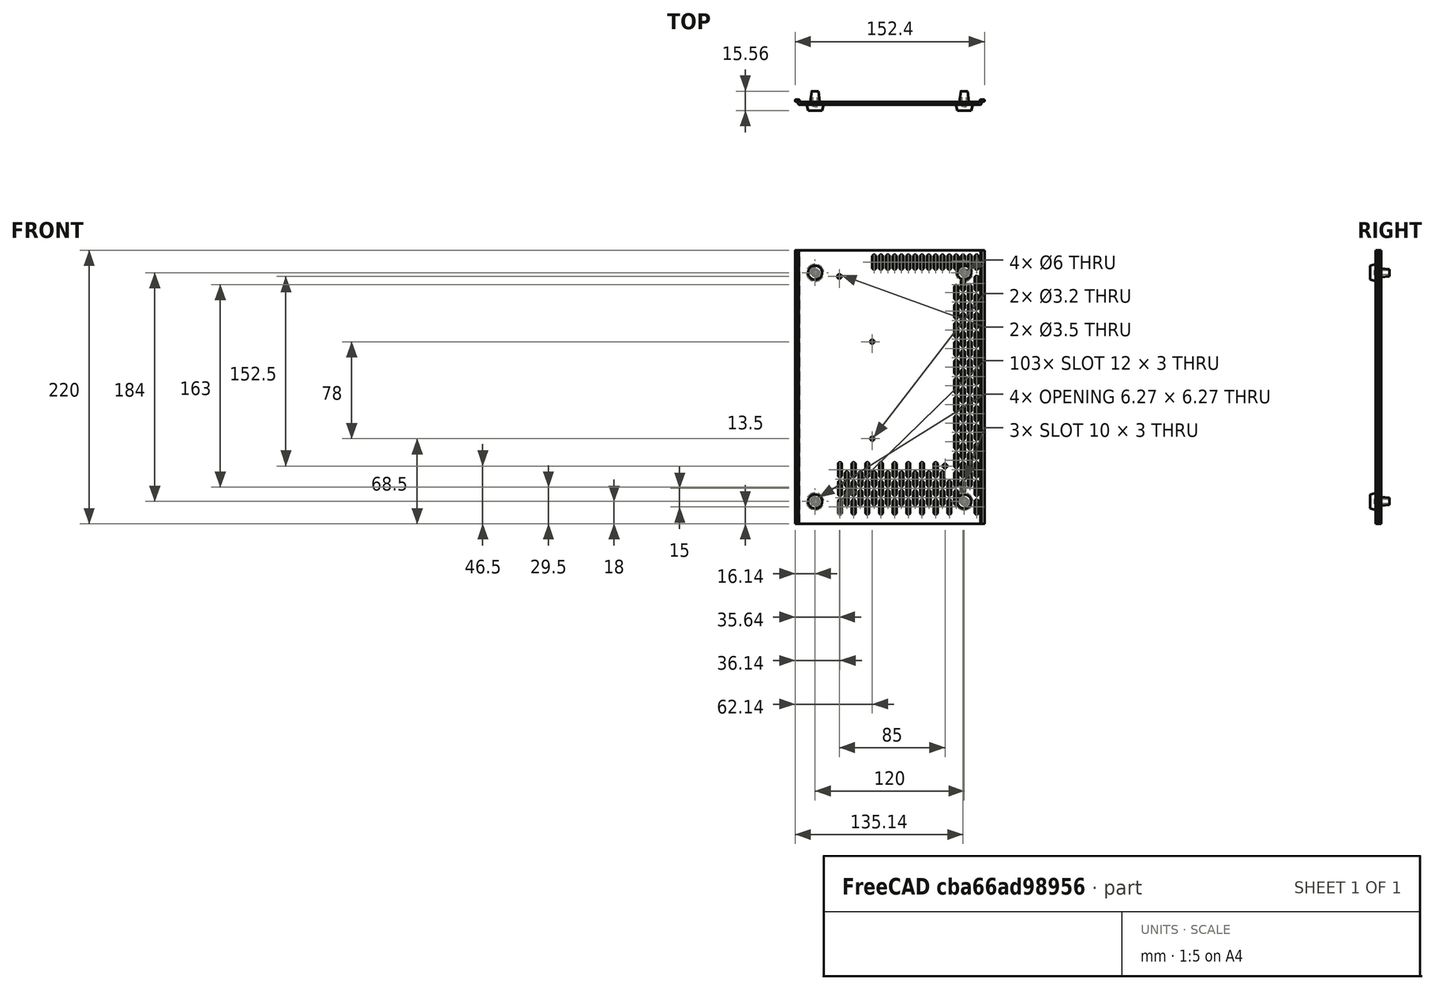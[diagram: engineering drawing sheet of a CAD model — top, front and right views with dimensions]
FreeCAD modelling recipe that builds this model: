
FCSTD DOCUMENT  (FreeCAD 0.19R)
Label: 3d_assm_bottomplate_w_feet
License: All rights reserved
LicenseURL: http://en.wikipedia.org/wiki/All_rights_reserved
objects: Sketcher::SketchObject×5, Part::Feature×5, App::DocumentObjectGroup×1
note: 10 computed .brp shape members not serialized (recipe doc carries the construction recipe); baked Part::Feature solids carry a one-line shape summary decoded from their .brp

FEATURE [Sketcher::SketchObject] Sketch008  label="Sketch008-Front_vent_slots"
  FullyConstrained = true
  MapMode = 5
  Placement = pos=(-1.0955e-12,2.25,0) rot=(0,0.707107,0.707107;3.14159rad)
  sketch-geometry (112):
    g0: LineSegment StartX=26 StartY=105 StartZ=0 EndX=-70 EndY=105 EndZ=0
    g1: LineSegment StartX=-70 StartY=96 StartZ=0 EndX=26 EndY=96 EndZ=0
    g2: LineSegment StartX=-70 StartY=105 StartZ=0 EndX=-70 EndY=96 EndZ=0
    g3: LineSegment StartX=-64.5 StartY=105 StartZ=0 EndX=-64.5 EndY=96 EndZ=0
    g4: LineSegment StartX=-70 StartY=105 StartZ=0 EndX=-64.5 EndY=105 EndZ=0
    g5: LineSegment StartX=-59 StartY=105 StartZ=0 EndX=-59 EndY=96 EndZ=0
    g6: LineSegment StartX=-64.5 StartY=105 StartZ=0 EndX=-59 EndY=105 EndZ=0
    g7: LineSegment StartX=-53.5 StartY=105 StartZ=0 EndX=-53.5 EndY=96 EndZ=0
    g8: LineSegment StartX=-59 StartY=105 StartZ=0 EndX=-53.5 EndY=105 EndZ=0
    g9: LineSegment StartX=-48 StartY=105 StartZ=0 EndX=-48 EndY=96 EndZ=0
    g10: LineSegment StartX=-53.5 StartY=105 StartZ=0 EndX=-48 EndY=105 EndZ=0
    g11: LineSegment StartX=-42.5 StartY=105 StartZ=0 EndX=-42.5 EndY=96 EndZ=0
    g12: LineSegment StartX=-48 StartY=105 StartZ=0 EndX=-42.5 EndY=105 EndZ=0
    g13: LineSegment StartX=-37 StartY=105 StartZ=0 EndX=-37 EndY=96 EndZ=0
    g14: LineSegment StartX=-42.5 StartY=105 StartZ=0 EndX=-37 EndY=105 EndZ=0
    g15: LineSegment StartX=-31.5 StartY=105 StartZ=0 EndX=-31.5 EndY=96 EndZ=0
    g16: LineSegment StartX=-37 StartY=105 StartZ=0 EndX=-31.5 EndY=105 EndZ=0
    g17: LineSegment StartX=-26 StartY=105 StartZ=0 EndX=-26 EndY=96 EndZ=0
    g18: LineSegment StartX=-31.5 StartY=105 StartZ=0 EndX=-26 EndY=105 EndZ=0
    g19: LineSegment StartX=-20.5 StartY=105 StartZ=0 EndX=-20.5 EndY=96 EndZ=0
    g20: LineSegment StartX=-26 StartY=105 StartZ=0 EndX=-20.5 EndY=105 EndZ=0
    g21: LineSegment StartX=-15 StartY=105 StartZ=0 EndX=-15 EndY=96 EndZ=0
    g22: LineSegment StartX=-20.5 StartY=105 StartZ=0 EndX=-15 EndY=105 EndZ=0
    g23: LineSegment StartX=-9.5 StartY=105 StartZ=0 EndX=-9.5 EndY=96 EndZ=0
    g24: LineSegment StartX=-15 StartY=105 StartZ=0 EndX=-9.5 EndY=105 EndZ=0
    g25: LineSegment StartX=-4 StartY=105 StartZ=0 EndX=-4 EndY=96 EndZ=0
    g26: LineSegment StartX=-9.5 StartY=105 StartZ=0 EndX=-4 EndY=105 EndZ=0
    g27: LineSegment StartX=1.5 StartY=105 StartZ=0 EndX=1.5 EndY=96 EndZ=0
    g28: LineSegment StartX=-4 StartY=105 StartZ=0 EndX=1.5 EndY=105 EndZ=0
    g29: LineSegment StartX=7 StartY=105 StartZ=0 EndX=7 EndY=96 EndZ=0
    g30: LineSegment StartX=1.5 StartY=105 StartZ=0 EndX=7 EndY=105 EndZ=0
    g31: LineSegment StartX=12.5 StartY=105 StartZ=0 EndX=12.5 EndY=96 EndZ=0
    g32: LineSegment StartX=7 StartY=105 StartZ=0 EndX=12.5 EndY=105 EndZ=0
    g33: ArcOfCircle CenterX=-70 CenterY=105 CenterZ=0 NormalX=0 NormalY=0 NormalZ=1 AngleXU=0 Radius=1.5 StartAngle=-3.6e-15 EndAngle=3.14159
    g34: ArcOfCircle CenterX=-70 CenterY=96 CenterZ=0 NormalX=0 NormalY=0 NormalZ=1 AngleXU=0 Radius=1.5 StartAngle=3.14159 EndAngle=6.28319
    g35: LineSegment StartX=-71.5 StartY=105 StartZ=0 EndX=-71.5 EndY=96 EndZ=0
    g36: LineSegment StartX=-68.5 StartY=105 StartZ=0 EndX=-68.5 EndY=96 EndZ=0
    g37: ArcOfCircle CenterX=-64.5 CenterY=105 CenterZ=0 NormalX=0 NormalY=0 NormalZ=1 AngleXU=0 Radius=1.5 StartAngle=4.5e-15 EndAngle=3.14159
    g38: ArcOfCircle CenterX=-64.5 CenterY=96 CenterZ=0 NormalX=0 NormalY=0 NormalZ=1 AngleXU=0 Radius=1.5 StartAngle=3.14159 EndAngle=6.28319
    g39: LineSegment StartX=-66 StartY=105 StartZ=0 EndX=-66 EndY=96 EndZ=0
    g40: LineSegment StartX=-63 StartY=105 StartZ=0 EndX=-63 EndY=96 EndZ=0
    g41: LineSegment StartX=-68.5 StartY=105 StartZ=0 EndX=-63 EndY=105 EndZ=0
    g42: ArcOfCircle CenterX=-59 CenterY=105 CenterZ=0 NormalX=0 NormalY=0 NormalZ=1 AngleXU=0 Radius=1.5 StartAngle=3.9e-15 EndAngle=3.14159
    g43: ArcOfCircle CenterX=-59 CenterY=98 CenterZ=0 NormalX=0 NormalY=0 NormalZ=1 AngleXU=0 Radius=1.5 StartAngle=3.14159 EndAngle=6.28319
    g44: LineSegment StartX=-60.5 StartY=105 StartZ=0 EndX=-60.5 EndY=98 EndZ=0
    g45: LineSegment StartX=-57.5 StartY=105 StartZ=0 EndX=-57.5 EndY=98 EndZ=0
    g46: LineSegment StartX=-63 StartY=105 StartZ=0 EndX=-57.5 EndY=105 EndZ=0
    g47: ArcOfCircle CenterX=-53.5 CenterY=105 CenterZ=0 NormalX=0 NormalY=0 NormalZ=1 AngleXU=0 Radius=1.5 StartAngle=3e-16 EndAngle=3.14159
    g48: ArcOfCircle CenterX=-53.5 CenterY=96 CenterZ=0 NormalX=0 NormalY=0 NormalZ=1 AngleXU=0 Radius=1.5 StartAngle=3.14159 EndAngle=6.28319
    g49: LineSegment StartX=-55 StartY=105 StartZ=0 EndX=-55 EndY=96 EndZ=0
    g50: LineSegment StartX=-52 StartY=105 StartZ=0 EndX=-52 EndY=96 EndZ=0
    g51: LineSegment StartX=-57.5 StartY=105 StartZ=0 EndX=-52 EndY=105 EndZ=0
    g52: ArcOfCircle CenterX=-48 CenterY=105 CenterZ=0 NormalX=0 NormalY=0 NormalZ=1 AngleXU=0 Radius=1.5 StartAngle=-2.7e-15 EndAngle=3.14159
    g53: ArcOfCircle CenterX=-48 CenterY=96 CenterZ=0 NormalX=0 NormalY=0 NormalZ=1 AngleXU=0 Radius=1.5 StartAngle=3.14159 EndAngle=6.28319
    g54: LineSegment StartX=-49.5 StartY=105 StartZ=0 EndX=-49.5 EndY=96 EndZ=0
    g55: LineSegment StartX=-46.5 StartY=105 StartZ=0 EndX=-46.5 EndY=96 EndZ=0
    g56: LineSegment StartX=-52 StartY=105 StartZ=0 EndX=-46.5 EndY=105 EndZ=0
    g57: ArcOfCircle CenterX=-42.5 CenterY=105 CenterZ=0 NormalX=0 NormalY=0 NormalZ=1 AngleXU=0 Radius=1.5 StartAngle=1.8e-15 EndAngle=3.14159
    g58: ArcOfCircle CenterX=-42.5 CenterY=96 CenterZ=0 NormalX=0 NormalY=0 NormalZ=1 AngleXU=0 Radius=1.5 StartAngle=3.14159 EndAngle=6.28319
    g59: LineSegment StartX=-44 StartY=105 StartZ=0 EndX=-44 EndY=96 EndZ=0
    g60: LineSegment StartX=-41 StartY=105 StartZ=0 EndX=-41 EndY=96 EndZ=0
    g61: LineSegment StartX=-46.5 StartY=105 StartZ=0 EndX=-41 EndY=105 EndZ=0
    g62: ArcOfCircle CenterX=-37 CenterY=105 CenterZ=0 NormalX=0 NormalY=0 NormalZ=1 AngleXU=0 Radius=1.5 StartAngle=-9e-16 EndAngle=3.14159
    g63: ArcOfCircle CenterX=-37 CenterY=96 CenterZ=0 NormalX=0 NormalY=0 NormalZ=1 AngleXU=0 Radius=1.5 StartAngle=3.14159 EndAngle=6.28319
    g64: LineSegment StartX=-38.5 StartY=105 StartZ=0 EndX=-38.5 EndY=96 EndZ=0
    g65: LineSegment StartX=-35.5 StartY=105 StartZ=0 EndX=-35.5 EndY=96 EndZ=0
    g66: LineSegment StartX=-41 StartY=105 StartZ=0 EndX=-35.5 EndY=105 EndZ=0
    g67: ArcOfCircle CenterX=-31.5 CenterY=105 CenterZ=0 NormalX=0 NormalY=0 NormalZ=1 AngleXU=0 Radius=1.5 StartAngle=-2.7e-15 EndAngle=3.14159
    g68: ArcOfCircle CenterX=-31.5 CenterY=96 CenterZ=0 NormalX=0 NormalY=0 NormalZ=1 AngleXU=0 Radius=1.5 StartAngle=3.14159 EndAngle=6.28319
    g69: LineSegment StartX=-33 StartY=105 StartZ=0 EndX=-33 EndY=96 EndZ=0
    g70: LineSegment StartX=-30 StartY=105 StartZ=0 EndX=-30 EndY=96 EndZ=0
    g71: LineSegment StartX=-35.5 StartY=105 StartZ=0 EndX=-30 EndY=105 EndZ=0
    g72: ArcOfCircle CenterX=-26 CenterY=105 CenterZ=0 NormalX=0 NormalY=0 NormalZ=1 AngleXU=0 Radius=1.5 StartAngle=-2.7e-15 EndAngle=3.14159
    g73: ArcOfCircle CenterX=-26 CenterY=96 CenterZ=0 NormalX=0 NormalY=0 NormalZ=1 AngleXU=0 Radius=1.5 StartAngle=3.14159 EndAngle=6.28319
    g74: LineSegment StartX=-27.5 StartY=105 StartZ=0 EndX=-27.5 EndY=96 EndZ=0
    g75: LineSegment StartX=-24.5 StartY=105 StartZ=0 EndX=-24.5 EndY=96 EndZ=0
    g76: LineSegment StartX=-30 StartY=105 StartZ=0 EndX=-24.5 EndY=105 EndZ=0
    g77: ArcOfCircle CenterX=-20.5 CenterY=105 CenterZ=0 NormalX=0 NormalY=0 NormalZ=1 AngleXU=0 Radius=1.5 StartAngle=-3.6e-15 EndAngle=3.14159
    g78: ArcOfCircle CenterX=-20.5 CenterY=96 CenterZ=0 NormalX=0 NormalY=0 NormalZ=1 AngleXU=0 Radius=1.5 StartAngle=3.14159 EndAngle=6.28319
    g79: LineSegment StartX=-22 StartY=105 StartZ=0 EndX=-22 EndY=96 EndZ=0
    g80: LineSegment StartX=-19 StartY=105 StartZ=0 EndX=-19 EndY=96 EndZ=0
    g81: LineSegment StartX=-24.5 StartY=105 StartZ=0 EndX=-19 EndY=105 EndZ=0
    g82: ArcOfCircle CenterX=-15 CenterY=105 CenterZ=0 NormalX=0 NormalY=0 NormalZ=1 AngleXU=0 Radius=1.5 StartAngle=2.4e-15 EndAngle=3.14159
    g83: ArcOfCircle CenterX=-15 CenterY=96 CenterZ=0 NormalX=0 NormalY=0 NormalZ=1 AngleXU=0 Radius=1.5 StartAngle=3.14159 EndAngle=6.28319
    g84: LineSegment StartX=-16.5 StartY=105 StartZ=0 EndX=-16.5 EndY=96 EndZ=0
    g85: LineSegment StartX=-13.5 StartY=105 StartZ=0 EndX=-13.5 EndY=96 EndZ=0
    g86: LineSegment StartX=-19 StartY=105 StartZ=0 EndX=-13.5 EndY=105 EndZ=0
    g87: ArcOfCircle CenterX=-9.5 CenterY=105 CenterZ=0 NormalX=0 NormalY=0 NormalZ=1 AngleXU=0 Radius=1.5 StartAngle=2.7e-15 EndAngle=3.14159
    g88: ArcOfCircle CenterX=-9.5 CenterY=96 CenterZ=0 NormalX=0 NormalY=0 NormalZ=1 AngleXU=0 Radius=1.5 StartAngle=3.14159 EndAngle=6.28319
    g89: LineSegment StartX=-11 StartY=105 StartZ=0 EndX=-11 EndY=96 EndZ=0
    g90: LineSegment StartX=-8 StartY=105 StartZ=0 EndX=-8 EndY=96 EndZ=0
    g91: LineSegment StartX=-13.5 StartY=105 StartZ=0 EndX=-8 EndY=105 EndZ=0
    g92: ArcOfCircle CenterX=-4 CenterY=105 CenterZ=0 NormalX=0 NormalY=0 NormalZ=1 AngleXU=0 Radius=1.5 StartAngle=3e-15 EndAngle=3.14159
    g93: ArcOfCircle CenterX=-4 CenterY=96 CenterZ=0 NormalX=0 NormalY=0 NormalZ=1 AngleXU=0 Radius=1.5 StartAngle=3.14159 EndAngle=6.28319
    g94: LineSegment StartX=-5.5 StartY=105 StartZ=0 EndX=-5.5 EndY=96 EndZ=0
    g95: LineSegment StartX=-2.5 StartY=105 StartZ=0 EndX=-2.5 EndY=96 EndZ=0
    g96: LineSegment StartX=-8 StartY=105 StartZ=0 EndX=-2.5 EndY=105 EndZ=0
    g97: ArcOfCircle CenterX=1.5 CenterY=105 CenterZ=0 NormalX=0 NormalY=0 NormalZ=1 AngleXU=0 Radius=1.5 StartAngle=1.8e-15 EndAngle=3.14159
    g98: ArcOfCircle CenterX=1.5 CenterY=96 CenterZ=0 NormalX=0 NormalY=0 NormalZ=1 AngleXU=0 Radius=1.5 StartAngle=3.14159 EndAngle=6.28319
    g99: LineSegment StartX=6e-15 StartY=105 StartZ=0 EndX=6e-15 EndY=96 EndZ=0
    g100: LineSegment StartX=3 StartY=105 StartZ=0 EndX=3 EndY=96 EndZ=0
    g101: LineSegment StartX=-2.5 StartY=105 StartZ=0 EndX=3 EndY=105 EndZ=0
    g102: ArcOfCircle CenterX=7 CenterY=105 CenterZ=0 NormalX=0 NormalY=0 NormalZ=1 AngleXU=0 Radius=1.5 StartAngle=-4.4e-15 EndAngle=3.14159
    g103: ArcOfCircle CenterX=7 CenterY=96 CenterZ=0 NormalX=0 NormalY=0 NormalZ=1 AngleXU=0 Radius=1.5 StartAngle=3.14159 EndAngle=6.28319
    g104: LineSegment StartX=5.5 StartY=105 StartZ=0 EndX=5.5 EndY=96 EndZ=0
    g105: LineSegment StartX=8.5 StartY=105 StartZ=0 EndX=8.5 EndY=96 EndZ=0
    g106: LineSegment StartX=3 StartY=105 StartZ=0 EndX=8.5 EndY=105 EndZ=0
    g107: ArcOfCircle CenterX=12.5 CenterY=105 CenterZ=0 NormalX=0 NormalY=0 NormalZ=1 AngleXU=0 Radius=1.5 StartAngle=2.7e-15 EndAngle=3.14159
    g108: ArcOfCircle CenterX=12.5 CenterY=96 CenterZ=0 NormalX=0 NormalY=0 NormalZ=1 AngleXU=0 Radius=1.5 StartAngle=3.14159 EndAngle=6.28319
    g109: LineSegment StartX=11 StartY=105 StartZ=0 EndX=11 EndY=96 EndZ=0
    g110: LineSegment StartX=14 StartY=105 StartZ=0 EndX=14 EndY=96 EndZ=0
    g111: LineSegment StartX=8.5 StartY=105 StartZ=0 EndX=14 EndY=105 EndZ=0
  constraints (289):
    c: Horizontal(g0)
    c: Horizontal(g1)
    c: DistanceX(g0,g0) = 96
    c: DistanceX(g0,g-1) = 70
    c: Equal(g0,g1)
    c: Vertical(g1,g0)
    c: DistanceY(g1,g0) = 9
    c: Coincident(g2,g0)
    c: Coincident(g2,g1)
    c: Vertical(g3)
    c: Coincident(g2,g4)
    c: Coincident(g3,g4)
    c: Distance(g4) = 5.5
    c: Vertical(g5)
    c: Coincident(g3,g6)
    c: Coincident(g5,g6)
    c: Equal(g4,g6)
    c: Parallel(g6,g4)
    c: Vertical(g7)
    c: Coincident(g5,g8)
    c: Coincident(g7,g8)
    c: Equal(g4,g8)
    c: Parallel(g8,g4)
    c: Vertical(g9)
    c: Coincident(g7,g10)
    c: Coincident(g9,g10)
    c: Equal(g4,g10)
    c: Parallel(g10,g4)
    c: Vertical(g11)
    c: Coincident(g9,g12)
    c: Coincident(g11,g12)
    c: Equal(g4,g12)
    c: Parallel(g12,g4)
    c: Vertical(g13)
    c: Coincident(g11,g14)
    c: Coincident(g13,g14)
    c: Equal(g4,g14)
    c: Parallel(g14,g4)
    c: Vertical(g15)
    c: Coincident(g13,g16)
    c: Coincident(g15,g16)
    c: Equal(g4,g16)
    c: Parallel(g16,g4)
    c: Vertical(g17)
    c: Coincident(g15,g18)
    c: Coincident(g17,g18)
    c: Equal(g4,g18)
    c: Parallel(g18,g4)
    c: Vertical(g19)
    c: Coincident(g17,g20)
    c: Coincident(g19,g20)
    c: Equal(g4,g20)
    c: Parallel(g20,g4)
    c: Vertical(g21)
    c: Coincident(g19,g22)
    c: Coincident(g21,g22)
    c: Equal(g4,g22)
    c: Parallel(g22,g4)
    c: Vertical(g23)
    c: Coincident(g21,g24)
    c: Coincident(g23,g24)
    c: Equal(g4,g24)
    c: Parallel(g24,g4)
    c: Vertical(g25)
    c: Coincident(g23,g26)
    c: Coincident(g25,g26)
    c: Equal(g4,g26)
    c: Parallel(g26,g4)
    c: Vertical(g27)
    c: Coincident(g25,g28)
    c: Coincident(g27,g28)
    c: Equal(g4,g28)
    c: Parallel(g28,g4)
    c: Vertical(g29)
    c: Coincident(g27,g30)
    c: Coincident(g29,g30)
    c: Equal(g4,g30)
    c: Parallel(g30,g4)
    c: Vertical(g31)
    c: Coincident(g29,g32)
    c: Coincident(g31,g32)
    c: Equal(g4,g32)
    c: Parallel(g32,g4)
    c: Horizontal(g1,g3)
    c: Horizontal(g3,g5)
    c: Horizontal(g5,g7)
    c: Horizontal(g7,g9)
    c: Horizontal(g9,g11)
    c: Horizontal(g11,g13)
    c: Horizontal(g13,g15)
    c: Horizontal(g15,g17)
    c: Horizontal(g17,g19)
    c: Horizontal(g19,g21)
    c: Horizontal(g21,g23)
    c: Horizontal(g23,g25)
    c: Horizontal(g25,g27)
    c: Horizontal(g27,g29)
    c: Horizontal(g29,g31)
    c: Angle(g26) = 0
    c: Tangent(g33,g36) = 1.5708
    c: Tangent(g33,g35) = -1.5708
    c: Tangent(g35,g34) = -1.5708
    c: Tangent(g36,g34) = 1.5708
    c: Vertical(g35)
    c: Equal(g33,g34)
    c: Coincident(g33,g0)
    c: DistanceX(g33,g33) = 3
    c: Tangent(g37,g40) = 1.5708
    c: Tangent(g37,g39) = -1.5708
    c: Tangent(g39,g38) = -1.5708
    c: Tangent(g40,g38) = 1.5708
    c: Vertical(g39)
    c: Equal(g37,g38)
    c: Equal(g33,g37) = 3
    c: Coincident(g33,g41)
    c: Coincident(g37,g41)
    c: Distance(g41) = 5.5
    c: Angle(g41) = 0
    c: Tangent(g42,g45) = 1.5708
    c: Tangent(g42,g44) = -1.5708
    c: Tangent(g44,g43) = -1.5708
    c: Tangent(g45,g43) = 1.5708
    c: Vertical(g44)
    c: Equal(g42,g43)
    c: Equal(g33,g42) = 3
    c: Coincident(g37,g46)
    c: Coincident(g42,g46)
    c: Equal(g41,g46)
    c: Parallel(g46,g41)
    c: Tangent(g47,g50) = 1.5708
    c: Tangent(g47,g49) = -1.5708
    c: Tangent(g49,g48) = -1.5708
    c: Tangent(g50,g48) = 1.5708
    c: Vertical(g49)
    c: Equal(g47,g48)
    c: Equal(g33,g47) = 3
    c: Coincident(g42,g51)
    c: Coincident(g47,g51)
    c: Equal(g41,g51)
    c: Parallel(g51,g41)
    c: Tangent(g52,g55) = 1.5708
    c: Tangent(g52,g54) = -1.5708
    c: Tangent(g54,g53) = -1.5708
    c: Tangent(g55,g53) = 1.5708
    c: Vertical(g54)
    c: Equal(g52,g53)
    c: Equal(g33,g52) = 3
    c: Coincident(g47,g56)
    c: Coincident(g52,g56)
    c: Equal(g41,g56)
    c: Parallel(g56,g41)
    c: Tangent(g57,g60) = 1.5708
    c: Tangent(g57,g59) = -1.5708
    c: Tangent(g59,g58) = -1.5708
    c: Tangent(g60,g58) = 1.5708
    c: Vertical(g59)
    c: Equal(g57,g58)
    c: Equal(g33,g57) = 3
    c: Coincident(g52,g61)
    c: Coincident(g57,g61)
    c: Equal(g41,g61)
    c: Parallel(g61,g41)
    c: Tangent(g62,g65) = 1.5708
    c: Tangent(g62,g64) = -1.5708
    c: Tangent(g64,g63) = -1.5708
    c: Tangent(g65,g63) = 1.5708
    c: Vertical(g64)
    c: Equal(g62,g63)
    c: Equal(g33,g62) = 3
    c: Coincident(g57,g66)
    c: Coincident(g62,g66)
    c: Equal(g41,g66)
    c: Parallel(g66,g41)
    c: Tangent(g67,g70) = 1.5708
    c: Tangent(g67,g69) = -1.5708
    c: Tangent(g69,g68) = -1.5708
    c: Tangent(g70,g68) = 1.5708
    c: Vertical(g69)
    c: Equal(g67,g68)
    c: Equal(g33,g67) = 3
    c: Coincident(g62,g71)
    c: Coincident(g67,g71)
    c: Equal(g41,g71)
    c: Parallel(g71,g41)
    c: Tangent(g72,g75) = 1.5708
    c: Tangent(g72,g74) = -1.5708
    c: Tangent(g74,g73) = -1.5708
    c: Tangent(g75,g73) = 1.5708
    c: Vertical(g74)
    c: Equal(g72,g73)
    c: Equal(g33,g72) = 3
    c: Coincident(g67,g76)
    c: Coincident(g72,g76)
    c: Equal(g41,g76)
    c: Parallel(g76,g41)
    c: Tangent(g77,g80) = 1.5708
    c: Tangent(g77,g79) = -1.5708
    c: Tangent(g79,g78) = -1.5708
    c: Tangent(g80,g78) = 1.5708
    c: Vertical(g79)
    c: Equal(g77,g78)
    c: Equal(g33,g77) = 3
    c: Coincident(g72,g81)
    c: Coincident(g77,g81)
    c: Equal(g41,g81)
    c: Parallel(g81,g41)
    c: Tangent(g82,g85) = 1.5708
    c: Tangent(g82,g84) = -1.5708
    c: Tangent(g84,g83) = -1.5708
    c: Tangent(g85,g83) = 1.5708
    c: Vertical(g84)
    c: Equal(g82,g83)
    c: Equal(g33,g82) = 3
    c: Coincident(g77,g86)
    c: Coincident(g82,g86)
    c: Equal(g41,g86)
    c: Parallel(g86,g41)
    c: Tangent(g87,g90) = 1.5708
    c: Tangent(g87,g89) = -1.5708
    c: Tangent(g89,g88) = -1.5708
    c: Tangent(g90,g88) = 1.5708
    c: Vertical(g89)
    c: Equal(g87,g88)
    c: Equal(g33,g87) = 3
    c: Coincident(g82,g91)
    c: Coincident(g87,g91)
    c: Equal(g41,g91)
    c: Parallel(g91,g41)
    c: Tangent(g92,g95) = 1.5708
    c: Tangent(g92,g94) = -1.5708
    c: Tangent(g94,g93) = -1.5708
    c: Tangent(g95,g93) = 1.5708
    c: Vertical(g94)
    c: Equal(g92,g93)
    c: Equal(g33,g92) = 3
    c: Coincident(g87,g96)
    c: Coincident(g92,g96)
    c: Equal(g41,g96)
    c: Parallel(g96,g41)
    c: Tangent(g97,g100) = 1.5708
    c: Tangent(g97,g99) = -1.5708
    c: Tangent(g99,g98) = -1.5708
    c: Tangent(g100,g98) = 1.5708
    c: Vertical(g99)
    c: Equal(g97,g98)
    c: Equal(g33,g97) = 3
    c: Coincident(g92,g101)
    c: Coincident(g97,g101)
    c: Equal(g41,g101)
    c: Parallel(g101,g41)
    c: Tangent(g102,g105) = 1.5708
    c: Tangent(g102,g104) = -1.5708
    c: Tangent(g104,g103) = -1.5708
    c: Tangent(g105,g103) = 1.5708
    c: Vertical(g104)
    c: Equal(g102,g103)
    c: Equal(g33,g102) = 3
    c: Coincident(g97,g106)
    c: Coincident(g102,g106)
    c: Equal(g41,g106)
    c: Parallel(g106,g41)
    c: Tangent(g107,g110) = 1.5708
    c: Tangent(g107,g109) = -1.5708
    c: Tangent(g109,g108) = -1.5708
    c: Tangent(g110,g108) = 1.5708
    c: Vertical(g109)
    c: Equal(g107,g108)
    c: Equal(g33,g107) = 3
    c: Coincident(g102,g111)
    c: Coincident(g107,g111)
    c: Equal(g41,g111)
    c: Parallel(g111,g41)
    c: Horizontal(g48,g53)
    c: Horizontal(g53,g58)
    c: Horizontal(g58,g63)
    c: Horizontal(g63,g68)
    c: Horizontal(g68,g73)
    c: Horizontal(g73,g78)
    c: Horizontal(g78,g83)
    c: Horizontal(g83,g88)
    c: Horizontal(g88,g93)
    c: Horizontal(g93,g98)
    c: Horizontal(g98,g103)
    c: Horizontal(g103,g108)
    c: DistanceY(g-1,g0) = 105
    c: Horizontal(g108,g1)
    c: DistanceY(g38,g37) = 9
    c: Horizontal(g34,g48)
    c: DistanceY(g43,g42) = 7
FEATURE [Sketcher::SketchObject] Sketch009
  FullyConstrained = false
  MapMode = 5
  Placement = pos=(-1.0955e-12,2.25,0) rot=(0,0.707107,0.707107;3.14159rad)
  sketch-geometry (289):
    g0: LineSegment StartX=-70 StartY=73 StartZ=0 EndX=-31.4704 EndY=73 EndZ=0
    g1: LineSegment StartX=-68.5 StartY=64 StartZ=0 EndX=-33.9766 EndY=64 EndZ=0
    g2: LineSegment StartX=-64.5 StartY=80.5 StartZ=0 EndX=-38.6885 EndY=80.5 EndZ=0
    g3: LineSegment StartX=-63 StartY=71.5 StartZ=0 EndX=-33.4278 EndY=71.5 EndZ=0
    g4: ArcOfCircle CenterX=-70 CenterY=73 CenterZ=0 NormalX=0 NormalY=0 NormalZ=1 AngleXU=0 Radius=1.5 StartAngle=-1.8e-15 EndAngle=3.14159
    g5: ArcOfCircle CenterX=-70 CenterY=64 CenterZ=0 NormalX=0 NormalY=0 NormalZ=1 AngleXU=0 Radius=1.5 StartAngle=3.14159 EndAngle=6.28319
    g6: LineSegment StartX=-71.5 StartY=73 StartZ=0 EndX=-71.5 EndY=64 EndZ=0
    g7: LineSegment StartX=-68.5 StartY=73 StartZ=0 EndX=-68.5 EndY=64 EndZ=0
    g8: ArcOfCircle CenterX=-64.5 CenterY=80.5 CenterZ=0 NormalX=0 NormalY=0 NormalZ=1 AngleXU=0 Radius=1.5 StartAngle=3.5e-15 EndAngle=3.14159
    g9: ArcOfCircle CenterX=-64.5 CenterY=71.5 CenterZ=0 NormalX=0 NormalY=0 NormalZ=1 AngleXU=0 Radius=1.5 StartAngle=3.14159 EndAngle=6.28319
    g10: LineSegment StartX=-66 StartY=80.5 StartZ=0 EndX=-66 EndY=71.5 EndZ=0
    g11: LineSegment StartX=-63 StartY=80.5 StartZ=0 EndX=-63 EndY=71.5 EndZ=0
    g12: GeomPoint X=-59 Y=73 Z=0
    g13: GeomPoint X=-53.5 Y=80.5 Z=0
    g14: GeomPoint X=-57.5 Y=64 Z=0
    g15: GeomPoint X=-52 Y=71.5 Z=0
    g16: ArcOfCircle CenterX=-59 CenterY=73 CenterZ=0 NormalX=0 NormalY=0 NormalZ=1 AngleXU=0 Radius=1.5 StartAngle=4.2e-15 EndAngle=3.14159
    g17: ArcOfCircle CenterX=-59 CenterY=64 CenterZ=0 NormalX=0 NormalY=0 NormalZ=1 AngleXU=0 Radius=1.5 StartAngle=3.14159 EndAngle=6.28319
    g18: LineSegment StartX=-60.5 StartY=73 StartZ=0 EndX=-60.5 EndY=64 EndZ=0
    g19: LineSegment StartX=-57.5 StartY=73 StartZ=0 EndX=-57.5 EndY=64 EndZ=0
    g20: ArcOfCircle CenterX=-53.5 CenterY=80.5 CenterZ=0 NormalX=0 NormalY=0 NormalZ=1 AngleXU=0 Radius=1.5 StartAngle=-3.6e-15 EndAngle=3.14159
    g21: ArcOfCircle CenterX=-53.5 CenterY=71.5 CenterZ=0 NormalX=0 NormalY=0 NormalZ=1 AngleXU=0 Radius=1.5 StartAngle=3.14159 EndAngle=6.28319
    g22: LineSegment StartX=-55 StartY=80.5 StartZ=0 EndX=-55 EndY=71.5 EndZ=0
    g23: LineSegment StartX=-52 StartY=80.5 StartZ=0 EndX=-52 EndY=71.5 EndZ=0
    g24: LineSegment StartX=-70 StartY=58 StartZ=0 EndX=-31.4798 EndY=58 EndZ=0
    g25: LineSegment StartX=-68.5094 StartY=49 StartZ=0 EndX=-33.986 EndY=49 EndZ=0
    g26: LineSegment StartX=-64.5 StartY=65.5 StartZ=0 EndX=-35.5428 EndY=65.5 EndZ=0
    g27: LineSegment StartX=-63.0094 StartY=56.5 StartZ=0 EndX=-33.4372 EndY=56.5 EndZ=0
    g28: ArcOfCircle CenterX=-70 CenterY=58 CenterZ=0 NormalX=0 NormalY=0 NormalZ=1 AngleXU=0 Radius=1.5 StartAngle=1.9e-15 EndAngle=3.14159
    g29: ArcOfCircle CenterX=-70 CenterY=49 CenterZ=0 NormalX=0 NormalY=0 NormalZ=1 AngleXU=0 Radius=1.5 StartAngle=3.14159 EndAngle=6.28319
    g30: LineSegment StartX=-71.5 StartY=58 StartZ=0 EndX=-71.5 EndY=49 EndZ=0
    g31: LineSegment StartX=-68.5 StartY=58 StartZ=0 EndX=-68.5 EndY=49 EndZ=0
    g32: ArcOfCircle CenterX=-64.5 CenterY=65.5 CenterZ=0 NormalX=0 NormalY=0 NormalZ=1 AngleXU=0 Radius=1.5 StartAngle=3.5e-15 EndAngle=3.14159
    g33: ArcOfCircle CenterX=-64.5 CenterY=56.5 CenterZ=0 NormalX=0 NormalY=0 NormalZ=1 AngleXU=0 Radius=1.5 StartAngle=3.14159 EndAngle=6.28319
    g34: LineSegment StartX=-66 StartY=65.5 StartZ=0 EndX=-66 EndY=56.5 EndZ=0
    g35: LineSegment StartX=-63 StartY=65.5 StartZ=0 EndX=-63 EndY=56.5 EndZ=0
    g36: GeomPoint X=-59 Y=58 Z=0
    g37: GeomPoint X=-53.5 Y=65.5 Z=0
    g38: GeomPoint X=-57.5 Y=49 Z=0
    g39: GeomPoint X=-52 Y=56.5 Z=0
    g40: ArcOfCircle CenterX=-59 CenterY=58 CenterZ=0 NormalX=0 NormalY=0 NormalZ=1 AngleXU=0 Radius=1.5 StartAngle=5e-16 EndAngle=3.14159
    g41: ArcOfCircle CenterX=-59 CenterY=49 CenterZ=0 NormalX=0 NormalY=0 NormalZ=1 AngleXU=0 Radius=1.5 StartAngle=3.14159 EndAngle=6.28319
    g42: LineSegment StartX=-60.5 StartY=58 StartZ=0 EndX=-60.5 EndY=49 EndZ=0
    g43: LineSegment StartX=-57.5 StartY=58 StartZ=0 EndX=-57.5 EndY=49 EndZ=0
    g44: ArcOfCircle CenterX=-53.5 CenterY=65.5 CenterZ=0 NormalX=0 NormalY=0 NormalZ=1 AngleXU=0 Radius=1.5 StartAngle=3.4e-15 EndAngle=3.14159
    g45: ArcOfCircle CenterX=-53.5 CenterY=56.5 CenterZ=0 NormalX=0 NormalY=0 NormalZ=1 AngleXU=0 Radius=1.5 StartAngle=3.14159 EndAngle=6.28319
    g46: LineSegment StartX=-55 StartY=65.5 StartZ=0 EndX=-55 EndY=56.5 EndZ=0
    g47: LineSegment StartX=-52 StartY=65.5 StartZ=0 EndX=-52 EndY=56.5 EndZ=0
    g48: LineSegment StartX=-70 StartY=43 StartZ=0 EndX=-31.5851 EndY=43 EndZ=0
    g49: LineSegment StartX=-68.6147 StartY=34 StartZ=0 EndX=-34.0913 EndY=34 EndZ=0
    g50: LineSegment StartX=-64.5 StartY=50.5 StartZ=0 EndX=-33.8249 EndY=50.5 EndZ=0
    g51: LineSegment StartX=-63.1147 StartY=41.5 StartZ=0 EndX=-33.5425 EndY=41.5 EndZ=0
    g52: ArcOfCircle CenterX=-70 CenterY=43 CenterZ=0 NormalX=0 NormalY=0 NormalZ=1 AngleXU=0 Radius=1.5 StartAngle=1.9e-15 EndAngle=3.14159
    g53: ArcOfCircle CenterX=-70 CenterY=34 CenterZ=0 NormalX=0 NormalY=0 NormalZ=1 AngleXU=0 Radius=1.5 StartAngle=3.14159 EndAngle=6.28319
    g54: LineSegment StartX=-71.5 StartY=43 StartZ=0 EndX=-71.5 EndY=34 EndZ=0
    g55: LineSegment StartX=-68.5 StartY=43 StartZ=0 EndX=-68.5 EndY=34 EndZ=0
    g56: ArcOfCircle CenterX=-64.5 CenterY=50.5 CenterZ=0 NormalX=0 NormalY=0 NormalZ=1 AngleXU=0 Radius=1.5 StartAngle=-9e-16 EndAngle=3.14159
    g57: ArcOfCircle CenterX=-64.5 CenterY=41.5 CenterZ=0 NormalX=0 NormalY=0 NormalZ=1 AngleXU=0 Radius=1.5 StartAngle=3.14159 EndAngle=6.28319
    g58: LineSegment StartX=-66 StartY=50.5 StartZ=0 EndX=-66 EndY=41.5 EndZ=0
    g59: LineSegment StartX=-63 StartY=50.5 StartZ=0 EndX=-63 EndY=41.5 EndZ=0
    g60: GeomPoint X=-59 Y=43 Z=0
    g61: GeomPoint X=-53.5 Y=50.5 Z=0
    g62: GeomPoint X=-57.5 Y=34 Z=0
    g63: GeomPoint X=-52 Y=41.5 Z=0
    g64: ArcOfCircle CenterX=-59 CenterY=43 CenterZ=0 NormalX=0 NormalY=0 NormalZ=1 AngleXU=0 Radius=1.5 StartAngle=-1.8e-15 EndAngle=3.14159
    g65: ArcOfCircle CenterX=-59 CenterY=34 CenterZ=0 NormalX=0 NormalY=0 NormalZ=1 AngleXU=0 Radius=1.5 StartAngle=3.14159 EndAngle=6.28319
    g66: LineSegment StartX=-60.5 StartY=43 StartZ=0 EndX=-60.5 EndY=34 EndZ=0
    g67: LineSegment StartX=-57.5 StartY=43 StartZ=0 EndX=-57.5 EndY=34 EndZ=0
    g68: ArcOfCircle CenterX=-53.5 CenterY=50.5 CenterZ=0 NormalX=0 NormalY=0 NormalZ=1 AngleXU=0 Radius=1.5 StartAngle=1.1e-15 EndAngle=3.14159
    g69: ArcOfCircle CenterX=-53.5 CenterY=41.5 CenterZ=0 NormalX=0 NormalY=0 NormalZ=1 AngleXU=0 Radius=1.5 StartAngle=3.14159 EndAngle=6.28319
    g70: LineSegment StartX=-55 StartY=50.5 StartZ=0 EndX=-55 EndY=41.5 EndZ=0
    g71: LineSegment StartX=-52 StartY=50.5 StartZ=0 EndX=-52 EndY=41.5 EndZ=0
    g72: LineSegment StartX=-70 StartY=28 StartZ=0 EndX=-29.8333 EndY=28 EndZ=0
    g73: LineSegment StartX=-68.6242 StartY=19 StartZ=0 EndX=-34.1007 EndY=19 EndZ=0
    g74: LineSegment StartX=-64.5 StartY=35.5 StartZ=0 EndX=-35.3892 EndY=35.5 EndZ=0
    g75: LineSegment StartX=-63.1242 StartY=26.5 StartZ=0 EndX=-33.5519 EndY=26.5 EndZ=0
    g76: ArcOfCircle CenterX=-70 CenterY=28 CenterZ=0 NormalX=0 NormalY=0 NormalZ=1 AngleXU=0 Radius=1.5 StartAngle=1.1e-15 EndAngle=3.14159
    g77: ArcOfCircle CenterX=-70 CenterY=19 CenterZ=0 NormalX=0 NormalY=0 NormalZ=1 AngleXU=0 Radius=1.5 StartAngle=3.14159 EndAngle=6.28319
    g78: LineSegment StartX=-71.5 StartY=28 StartZ=0 EndX=-71.5 EndY=19 EndZ=0
    g79: LineSegment StartX=-68.5 StartY=28 StartZ=0 EndX=-68.5 EndY=19 EndZ=0
    g80: ArcOfCircle CenterX=-64.5 CenterY=35.5 CenterZ=0 NormalX=0 NormalY=0 NormalZ=1 AngleXU=0 Radius=1.5 StartAngle=1.1e-15 EndAngle=3.14159
    g81: ArcOfCircle CenterX=-64.5 CenterY=26.5 CenterZ=0 NormalX=0 NormalY=0 NormalZ=1 AngleXU=0 Radius=1.5 StartAngle=3.14159 EndAngle=6.28319
    g82: LineSegment StartX=-66 StartY=35.5 StartZ=0 EndX=-66 EndY=26.5 EndZ=0
    g83: LineSegment StartX=-63 StartY=35.5 StartZ=0 EndX=-63 EndY=26.5 EndZ=0
    g84: GeomPoint X=-59 Y=28 Z=0
    g85: GeomPoint X=-53.5 Y=35.5 Z=0
    g86: GeomPoint X=-57.5 Y=19 Z=0
    g87: GeomPoint X=-52 Y=26.5 Z=0
    g88: ArcOfCircle CenterX=-59 CenterY=28 CenterZ=0 NormalX=0 NormalY=0 NormalZ=1 AngleXU=0 Radius=1.5 StartAngle=5e-16 EndAngle=3.14159
    g89: ArcOfCircle CenterX=-59 CenterY=19 CenterZ=0 NormalX=0 NormalY=0 NormalZ=1 AngleXU=0 Radius=1.5 StartAngle=3.14159 EndAngle=6.28319
    g90: LineSegment StartX=-60.5 StartY=28 StartZ=0 EndX=-60.5 EndY=19 EndZ=0
    g91: LineSegment StartX=-57.5 StartY=28 StartZ=0 EndX=-57.5 EndY=19 EndZ=0
    g92: ArcOfCircle CenterX=-53.5 CenterY=35.5 CenterZ=0 NormalX=0 NormalY=0 NormalZ=1 AngleXU=0 Radius=1.5 StartAngle=5e-16 EndAngle=3.14159
    g93: ArcOfCircle CenterX=-53.5 CenterY=26.5 CenterZ=0 NormalX=0 NormalY=0 NormalZ=1 AngleXU=0 Radius=1.5 StartAngle=3.14159 EndAngle=6.28319
    g94: LineSegment StartX=-55 StartY=35.5 StartZ=0 EndX=-55 EndY=26.5 EndZ=0
    g95: LineSegment StartX=-52 StartY=35.5 StartZ=0 EndX=-52 EndY=26.5 EndZ=0
    g96: LineSegment StartX=-70 StartY=13 StartZ=0 EndX=-24.2092 EndY=13 EndZ=0
    g97: LineSegment StartX=-54.4311 StartY=4 StartZ=0 EndX=-19.9077 EndY=4 EndZ=0
    g98: LineSegment StartX=-64.5 StartY=20.5 StartZ=0 EndX=-33.8444 EndY=20.5 EndZ=0
    g99: LineSegment StartX=-48.9311 StartY=11.5 StartZ=0 EndX=-19.3589 EndY=11.5 EndZ=0
    g100: ArcOfCircle CenterX=-70 CenterY=13 CenterZ=0 NormalX=0 NormalY=0 NormalZ=1 AngleXU=0 Radius=1.5 StartAngle=2e-16 EndAngle=3.14159
    g101: ArcOfCircle CenterX=-70 CenterY=4 CenterZ=0 NormalX=0 NormalY=0 NormalZ=1 AngleXU=0 Radius=1.5 StartAngle=3.14159 EndAngle=6.28319
    g102: LineSegment StartX=-71.5 StartY=13 StartZ=0 EndX=-71.5 EndY=4 EndZ=0
    g103: LineSegment StartX=-68.5 StartY=13 StartZ=0 EndX=-68.5 EndY=4 EndZ=0
    g104: ArcOfCircle CenterX=-64.5 CenterY=20.5 CenterZ=0 NormalX=0 NormalY=0 NormalZ=1 AngleXU=0 Radius=1.5 StartAngle=-9e-16 EndAngle=3.14159
    g105: ArcOfCircle CenterX=-64.5 CenterY=11.5 CenterZ=0 NormalX=0 NormalY=0 NormalZ=1 AngleXU=0 Radius=1.5 StartAngle=3.14159 EndAngle=6.28319
    g106: LineSegment StartX=-66 StartY=20.5 StartZ=0 EndX=-66 EndY=11.5 EndZ=0
    g107: LineSegment StartX=-63 StartY=20.5 StartZ=0 EndX=-63 EndY=11.5 EndZ=0
    g108: GeomPoint X=-59 Y=13 Z=0
    g109: GeomPoint X=-53.5 Y=20.5 Z=0
    g110: GeomPoint X=-57.5 Y=4 Z=0
    g111: GeomPoint X=-52 Y=11.5 Z=0
    g112: ArcOfCircle CenterX=-59 CenterY=13 CenterZ=0 NormalX=0 NormalY=0 NormalZ=1 AngleXU=0 Radius=1.5 StartAngle=1e-16 EndAngle=3.14159
    g113: ArcOfCircle CenterX=-59 CenterY=4 CenterZ=0 NormalX=0 NormalY=0 NormalZ=1 AngleXU=0 Radius=1.5 StartAngle=3.14159 EndAngle=6.28319
    g114: LineSegment StartX=-60.5 StartY=13 StartZ=0 EndX=-60.5 EndY=4 EndZ=0
    g115: LineSegment StartX=-57.5 StartY=13 StartZ=0 EndX=-57.5 EndY=4 EndZ=0
    g116: ArcOfCircle CenterX=-53.5 CenterY=20.5 CenterZ=0 NormalX=0 NormalY=0 NormalZ=1 AngleXU=0 Radius=1.5 StartAngle=1.1e-15 EndAngle=3.14159
    g117: ArcOfCircle CenterX=-53.5 CenterY=11.5 CenterZ=0 NormalX=0 NormalY=0 NormalZ=1 AngleXU=0 Radius=1.5 StartAngle=3.14159 EndAngle=6.28319
    g118: LineSegment StartX=-55 StartY=20.5 StartZ=0 EndX=-55 EndY=11.5 EndZ=0
    g119: LineSegment StartX=-52 StartY=20.5 StartZ=0 EndX=-52 EndY=11.5 EndZ=0
    g120: LineSegment StartX=-70 StartY=-2 StartZ=0 EndX=-17.4109 EndY=-2 EndZ=0
    g121: LineSegment StartX=-54.4405 StartY=-11 StartZ=0 EndX=-19.9171 EndY=-11 EndZ=0
    g122: LineSegment StartX=-64.5 StartY=5.5 StartZ=0 EndX=-21.2056 EndY=5.5 EndZ=0
    g123: LineSegment StartX=-48.9405 StartY=-3.5 StartZ=0 EndX=-19.3683 EndY=-3.5 EndZ=0
    g124: ArcOfCircle CenterX=-70 CenterY=-2 CenterZ=0 NormalX=0 NormalY=0 NormalZ=1 AngleXU=0 Radius=1.5 StartAngle=2e-16 EndAngle=3.14159
    g125: ArcOfCircle CenterX=-70 CenterY=-11 CenterZ=0 NormalX=0 NormalY=0 NormalZ=1 AngleXU=0 Radius=1.5 StartAngle=3.14159 EndAngle=6.28319
    g126: LineSegment StartX=-71.5 StartY=-2 StartZ=0 EndX=-71.5 EndY=-11 EndZ=0
    g127: LineSegment StartX=-68.5 StartY=-2 StartZ=0 EndX=-68.5 EndY=-11 EndZ=0
    g128: ArcOfCircle CenterX=-64.5 CenterY=5.5 CenterZ=0 NormalX=0 NormalY=0 NormalZ=1 AngleXU=0 Radius=1.5 StartAngle=1e-16 EndAngle=3.14159
    g129: ArcOfCircle CenterX=-64.5 CenterY=-3.5 CenterZ=0 NormalX=0 NormalY=0 NormalZ=1 AngleXU=0 Radius=1.5 StartAngle=3.14159 EndAngle=6.28319
    g130: LineSegment StartX=-66 StartY=5.5 StartZ=0 EndX=-66 EndY=-3.5 EndZ=0
    g131: LineSegment StartX=-63 StartY=5.5 StartZ=0 EndX=-63 EndY=-3.5 EndZ=0
    g132: GeomPoint X=-59 Y=-2 Z=0
    g133: GeomPoint X=-53.5 Y=5.5 Z=0
    g134: GeomPoint X=-57.5 Y=-11 Z=0
    g135: GeomPoint X=-52 Y=-3.5 Z=0
    g136: ArcOfCircle CenterX=-59 CenterY=-2 CenterZ=0 NormalX=0 NormalY=0 NormalZ=1 AngleXU=0 Radius=1.5 StartAngle=1e-16 EndAngle=3.14159
    g137: ArcOfCircle CenterX=-59 CenterY=-11 CenterZ=0 NormalX=0 NormalY=0 NormalZ=1 AngleXU=0 Radius=1.5 StartAngle=3.14159 EndAngle=6.28319
    g138: LineSegment StartX=-60.5 StartY=-2 StartZ=0 EndX=-60.5 EndY=-11 EndZ=0
    g139: LineSegment StartX=-57.5 StartY=-2 StartZ=0 EndX=-57.5 EndY=-11 EndZ=0
    g140: ArcOfCircle CenterX=-53.5 CenterY=5.5 CenterZ=0 NormalX=0 NormalY=0 NormalZ=1 AngleXU=0 Radius=1.5 StartAngle=1e-16 EndAngle=3.14159
    g141: ArcOfCircle CenterX=-53.5 CenterY=-3.5 CenterZ=0 NormalX=0 NormalY=0 NormalZ=1 AngleXU=0 Radius=1.5 StartAngle=3.14159 EndAngle=6.28319
    g142: LineSegment StartX=-55 StartY=5.5 StartZ=0 EndX=-55 EndY=-3.5 EndZ=0
    g143: LineSegment StartX=-52 StartY=5.5 StartZ=0 EndX=-52 EndY=-3.5 EndZ=0
    g144: LineSegment StartX=-70 StartY=-17 StartZ=0 EndX=-17.5162 EndY=-17 EndZ=0
    g145: LineSegment StartX=-54.5458 StartY=-26 StartZ=0 EndX=-20.0224 EndY=-26 EndZ=0
    g146: LineSegment StartX=-64.5 StartY=-9.5 StartZ=0 EndX=-19.756 EndY=-9.5 EndZ=0
    g147: LineSegment StartX=-49.0458 StartY=-18.5 StartZ=0 EndX=-19.4736 EndY=-18.5 EndZ=0
    g148: ArcOfCircle CenterX=-70 CenterY=-17 CenterZ=0 NormalX=0 NormalY=0 NormalZ=1 AngleXU=0 Radius=1.5 StartAngle=-9e-16 EndAngle=3.14159
    g149: ArcOfCircle CenterX=-70 CenterY=-26 CenterZ=0 NormalX=0 NormalY=0 NormalZ=1 AngleXU=0 Radius=1.5 StartAngle=3.14159 EndAngle=6.28319
    g150: LineSegment StartX=-71.5 StartY=-17 StartZ=0 EndX=-71.5 EndY=-26 EndZ=0
    g151: LineSegment StartX=-68.5 StartY=-17 StartZ=0 EndX=-68.5 EndY=-26 EndZ=0
    g152: ArcOfCircle CenterX=-64.5 CenterY=-9.5 CenterZ=0 NormalX=0 NormalY=0 NormalZ=1 AngleXU=0 Radius=1.5 StartAngle=6e-16 EndAngle=3.14159
    g153: ArcOfCircle CenterX=-64.5 CenterY=-18.5 CenterZ=0 NormalX=0 NormalY=0 NormalZ=1 AngleXU=0 Radius=1.5 StartAngle=3.14159 EndAngle=6.28319
    g154: LineSegment StartX=-66 StartY=-9.5 StartZ=0 EndX=-66 EndY=-18.5 EndZ=0
    g155: LineSegment StartX=-63 StartY=-9.5 StartZ=0 EndX=-63 EndY=-18.5 EndZ=0
    g156: GeomPoint X=-59 Y=-17 Z=0
    g157: GeomPoint X=-53.5 Y=-9.5 Z=0
    g158: GeomPoint X=-57.5 Y=-26 Z=0
    g159: GeomPoint X=-52 Y=-18.5 Z=0
    g160: ArcOfCircle CenterX=-59 CenterY=-17 CenterZ=0 NormalX=0 NormalY=0 NormalZ=1 AngleXU=0 Radius=1.5 StartAngle=-9e-16 EndAngle=3.14159
    g161: ArcOfCircle CenterX=-59 CenterY=-26 CenterZ=0 NormalX=0 NormalY=0 NormalZ=1 AngleXU=0 Radius=1.5 StartAngle=3.14159 EndAngle=6.28319
    g162: LineSegment StartX=-60.5 StartY=-17 StartZ=0 EndX=-60.5 EndY=-26 EndZ=0
    g163: LineSegment StartX=-57.5 StartY=-17 StartZ=0 EndX=-57.5 EndY=-26 EndZ=0
    g164: ArcOfCircle CenterX=-53.5 CenterY=-9.5 CenterZ=0 NormalX=0 NormalY=0 NormalZ=1 AngleXU=0 Radius=1.5 StartAngle=1e-16 EndAngle=3.14159
    g165: ArcOfCircle CenterX=-53.5 CenterY=-18.5 CenterZ=0 NormalX=0 NormalY=0 NormalZ=1 AngleXU=0 Radius=1.5 StartAngle=3.14159 EndAngle=6.28319
    g166: LineSegment StartX=-55 StartY=-9.5 StartZ=0 EndX=-55 EndY=-18.5 EndZ=0
    g167: LineSegment StartX=-52 StartY=-9.5 StartZ=0 EndX=-52 EndY=-18.5 EndZ=0
    g168: LineSegment StartX=-70 StartY=-32 StartZ=0 EndX=-15.7643 EndY=-32 EndZ=0
    g169: LineSegment StartX=-54.5552 StartY=-41 StartZ=0 EndX=-20.0318 EndY=-41 EndZ=0
    g170: LineSegment StartX=-64.5 StartY=-24.5 StartZ=0 EndX=-21.3203 EndY=-24.5 EndZ=0
    g171: LineSegment StartX=-49.0552 StartY=-33.5 StartZ=0 EndX=-19.483 EndY=-33.5 EndZ=0
    g172: ArcOfCircle CenterX=-70 CenterY=-32 CenterZ=0 NormalX=0 NormalY=0 NormalZ=1 AngleXU=0 Radius=1.5 StartAngle=1.1e-15 EndAngle=3.14159
    g173: ArcOfCircle CenterX=-70 CenterY=-41 CenterZ=0 NormalX=0 NormalY=0 NormalZ=1 AngleXU=0 Radius=1.5 StartAngle=3.14159 EndAngle=6.28319
    g174: LineSegment StartX=-71.5 StartY=-32 StartZ=0 EndX=-71.5 EndY=-41 EndZ=0
    g175: LineSegment StartX=-68.5 StartY=-32 StartZ=0 EndX=-68.5 EndY=-41 EndZ=0
    g176: ArcOfCircle CenterX=-64.5 CenterY=-24.5 CenterZ=0 NormalX=0 NormalY=0 NormalZ=1 AngleXU=0 Radius=1.5 StartAngle=1.1e-15 EndAngle=3.14159
    g177: ArcOfCircle CenterX=-64.5 CenterY=-33.5 CenterZ=0 NormalX=0 NormalY=0 NormalZ=1 AngleXU=0 Radius=1.5 StartAngle=3.14159 EndAngle=6.28319
    g178: LineSegment StartX=-66 StartY=-24.5 StartZ=0 EndX=-66 EndY=-33.5 EndZ=0
    g179: LineSegment StartX=-63 StartY=-24.5 StartZ=0 EndX=-63 EndY=-33.5 EndZ=0
    g180: GeomPoint X=-59 Y=-32 Z=0
    g181: GeomPoint X=-53.5 Y=-24.5 Z=0
    g182: GeomPoint X=-57.5 Y=-41 Z=0
    g183: GeomPoint X=-52 Y=-33.5 Z=0
    g184: ArcOfCircle CenterX=-59 CenterY=-32 CenterZ=0 NormalX=0 NormalY=0 NormalZ=1 AngleXU=0 Radius=1.5 StartAngle=-9e-16 EndAngle=3.14159
    g185: ArcOfCircle CenterX=-59 CenterY=-41 CenterZ=0 NormalX=0 NormalY=0 NormalZ=1 AngleXU=0 Radius=1.5 StartAngle=3.14159 EndAngle=6.28319
    g186: LineSegment StartX=-60.5 StartY=-32 StartZ=0 EndX=-60.5 EndY=-41 EndZ=0
    g187: LineSegment StartX=-57.5 StartY=-32 StartZ=0 EndX=-57.5 EndY=-41 EndZ=0
    g188: ArcOfCircle CenterX=-53.5 CenterY=-24.5 CenterZ=0 NormalX=0 NormalY=0 NormalZ=1 AngleXU=0 Radius=1.5 StartAngle=-9e-16 EndAngle=3.14159
    g189: ArcOfCircle CenterX=-53.5 CenterY=-33.5 CenterZ=0 NormalX=0 NormalY=0 NormalZ=1 AngleXU=0 Radius=1.5 StartAngle=3.14159 EndAngle=6.28319
    g190: LineSegment StartX=-55 StartY=-24.5 StartZ=0 EndX=-55 EndY=-33.5 EndZ=0
    g191: LineSegment StartX=-52 StartY=-24.5 StartZ=0 EndX=-52 EndY=-33.5 EndZ=0
    g192: GeomPoint X=-53.244 Y=-30.9002 Z=0
    g193: LineSegment StartX=-70 StartY=-47 StartZ=0 EndX=-46.1296 EndY=-47 EndZ=0
    g194: LineSegment StartX=-67.4613 StartY=-56 StartZ=0 EndX=-42.5684 EndY=-56 EndZ=0
    g195: LineSegment StartX=-64.5 StartY=-39.5 StartZ=0 EndX=-19.4999 EndY=-39.5 EndZ=0
    g196: LineSegment StartX=-48.7898 StartY=-48.5 StartZ=0 EndX=-42.8921 EndY=-48.5 EndZ=0
    g197: ArcOfCircle CenterX=-70 CenterY=-47 CenterZ=0 NormalX=0 NormalY=0 NormalZ=1 AngleXU=0 Radius=1.5 StartAngle=5e-16 EndAngle=3.14159
    g198: ArcOfCircle CenterX=-70 CenterY=-56 CenterZ=0 NormalX=0 NormalY=0 NormalZ=1 AngleXU=0 Radius=1.5 StartAngle=3.14159 EndAngle=6.28319
    g199: LineSegment StartX=-71.5 StartY=-47 StartZ=0 EndX=-71.5 EndY=-56 EndZ=0
    g200: LineSegment StartX=-68.5 StartY=-47 StartZ=0 EndX=-68.5 EndY=-56 EndZ=0
    g201: ArcOfCircle CenterX=-64.5 CenterY=-39.5 CenterZ=0 NormalX=0 NormalY=0 NormalZ=1 AngleXU=0 Radius=1.5 StartAngle=-1.8e-15 EndAngle=3.14159
    g202: ArcOfCircle CenterX=-64.5 CenterY=-48.5 CenterZ=0 NormalX=0 NormalY=0 NormalZ=1 AngleXU=0 Radius=1.5 StartAngle=3.14159 EndAngle=6.28319
    g203: LineSegment StartX=-66 StartY=-39.5 StartZ=0 EndX=-66 EndY=-48.5 EndZ=0
    g204: LineSegment StartX=-63 StartY=-39.5 StartZ=0 EndX=-63 EndY=-48.5 EndZ=0
    g205: GeomPoint X=-59 Y=-47 Z=0
    g206: GeomPoint X=-53.5 Y=-39.5 Z=0
    g207: GeomPoint X=-57.5 Y=-56 Z=0
    g208: GeomPoint X=-52 Y=-48.5 Z=0
    g209: ArcOfCircle CenterX=-59 CenterY=-47 CenterZ=0 NormalX=0 NormalY=0 NormalZ=1 AngleXU=0 Radius=1.5 StartAngle=6e-16 EndAngle=3.14159
    g210: ArcOfCircle CenterX=-59 CenterY=-56 CenterZ=0 NormalX=0 NormalY=0 NormalZ=1 AngleXU=0 Radius=1.5 StartAngle=3.14159 EndAngle=6.28319
    g211: LineSegment StartX=-60.5 StartY=-47 StartZ=0 EndX=-60.5 EndY=-56 EndZ=0
    g212: LineSegment StartX=-57.5 StartY=-47 StartZ=0 EndX=-57.5 EndY=-56 EndZ=0
    g213: ArcOfCircle CenterX=-53.5 CenterY=-39.5 CenterZ=0 NormalX=0 NormalY=0 NormalZ=1 AngleXU=0 Radius=1.5 StartAngle=-1.8e-15 EndAngle=3.14159
    g214: ArcOfCircle CenterX=-53.5 CenterY=-48.5 CenterZ=0 NormalX=0 NormalY=0 NormalZ=1 AngleXU=0 Radius=1.5 StartAngle=3.14159 EndAngle=6.28319
    g215: LineSegment StartX=-55 StartY=-39.5 StartZ=0 EndX=-55 EndY=-48.5 EndZ=0
    g216: LineSegment StartX=-52 StartY=-39.5 StartZ=0 EndX=-52 EndY=-48.5 EndZ=0
    g217: LineSegment StartX=-70 StartY=-62 StartZ=0 EndX=-42.3166 EndY=-62 EndZ=0
    g218: LineSegment StartX=-54.2992 StartY=-71 StartZ=0 EndX=-42.7122 EndY=-71 EndZ=0
    g219: LineSegment StartX=-64.5 StartY=-54.5 StartZ=0 EndX=-43.4677 EndY=-54.5 EndZ=0
    g220: LineSegment StartX=-48.7992 StartY=-63.5 StartZ=0 EndX=-42.4964 EndY=-63.5 EndZ=0
    g221: ArcOfCircle CenterX=-70 CenterY=-62 CenterZ=0 NormalX=0 NormalY=0 NormalZ=1 AngleXU=0 Radius=1.5 StartAngle=1.9e-15 EndAngle=3.14159
    g222: ArcOfCircle CenterX=-70 CenterY=-71 CenterZ=0 NormalX=0 NormalY=0 NormalZ=1 AngleXU=0 Radius=1.5 StartAngle=3.14159 EndAngle=6.28319
    g223: LineSegment StartX=-71.5 StartY=-62 StartZ=0 EndX=-71.5 EndY=-71 EndZ=0
    g224: LineSegment StartX=-68.5 StartY=-62 StartZ=0 EndX=-68.5 EndY=-71 EndZ=0
    g225: ArcOfCircle CenterX=-64.5 CenterY=-54.5 CenterZ=0 NormalX=0 NormalY=0 NormalZ=1 AngleXU=0 Radius=1.5 StartAngle=1.1e-15 EndAngle=3.14159
    g226: ArcOfCircle CenterX=-64.5 CenterY=-63.5 CenterZ=0 NormalX=0 NormalY=0 NormalZ=1 AngleXU=0 Radius=1.5 StartAngle=3.14159 EndAngle=6.28319
    g227: LineSegment StartX=-66 StartY=-54.5 StartZ=0 EndX=-66 EndY=-63.5 EndZ=0
    g228: LineSegment StartX=-63 StartY=-54.5 StartZ=0 EndX=-63 EndY=-63.5 EndZ=0
    g229: GeomPoint X=-59 Y=-62 Z=0
    g230: GeomPoint X=-53.5 Y=-54.5 Z=0
    g231: GeomPoint X=-57.5 Y=-71 Z=0
    g232: GeomPoint X=-52 Y=-63.5 Z=0
    g233: ArcOfCircle CenterX=-59 CenterY=-62 CenterZ=0 NormalX=0 NormalY=0 NormalZ=1 AngleXU=0 Radius=1.5 StartAngle=1.9e-15 EndAngle=3.14159
    g234: ArcOfCircle CenterX=-59 CenterY=-71 CenterZ=0 NormalX=0 NormalY=0 NormalZ=1 AngleXU=0 Radius=1.5 StartAngle=3.14159 EndAngle=6.28319
    g235: LineSegment StartX=-60.5 StartY=-62 StartZ=0 EndX=-60.5 EndY=-71 EndZ=0
    g236: LineSegment StartX=-57.5 StartY=-62 StartZ=0 EndX=-57.5 EndY=-71 EndZ=0
    g237: ArcOfCircle CenterX=-53.5 CenterY=-54.5 CenterZ=0 NormalX=0 NormalY=0 NormalZ=1 AngleXU=0 Radius=1.5 StartAngle=-9e-16 EndAngle=3.14159
    g238: ArcOfCircle CenterX=-53.5 CenterY=-63.5 CenterZ=0 NormalX=0 NormalY=0 NormalZ=1 AngleXU=0 Radius=1.5 StartAngle=3.14159 EndAngle=6.28319
    g239: LineSegment StartX=-55 StartY=-54.5 StartZ=0 EndX=-55 EndY=-63.5 EndZ=0
    g240: LineSegment StartX=-52 StartY=-54.5 StartZ=0 EndX=-52 EndY=-63.5 EndZ=0
    g241: LineSegment StartX=-70 StartY=-77 StartZ=0 EndX=-42.5299 EndY=-77 EndZ=0
    g242: LineSegment StartX=-54.5126 StartY=-86 StartZ=0 EndX=-42.9256 EndY=-86 EndZ=0
    g243: LineSegment StartX=-49.0126 StartY=-78.5 StartZ=0 EndX=-42.7098 EndY=-78.5 EndZ=0
    g244: ArcOfCircle CenterX=-70 CenterY=-77 CenterZ=0 NormalX=0 NormalY=0 NormalZ=1 AngleXU=0 Radius=1.5 StartAngle=1e-16 EndAngle=3.14159
    g245: ArcOfCircle CenterX=-70 CenterY=-86 CenterZ=0 NormalX=0 NormalY=0 NormalZ=1 AngleXU=0 Radius=1.5 StartAngle=3.14159 EndAngle=6.28319
    g246: LineSegment StartX=-71.5 StartY=-77 StartZ=0 EndX=-71.5 EndY=-86 EndZ=0
    g247: LineSegment StartX=-68.5 StartY=-77 StartZ=0 EndX=-68.5 EndY=-86 EndZ=0
    g248: ArcOfCircle CenterX=-64.5 CenterY=-78.5 CenterZ=0 NormalX=0 NormalY=0 NormalZ=1 AngleXU=0 Radius=1.5 StartAngle=3.14159 EndAngle=6.28319
    g249: GeomPoint X=-59 Y=-77 Z=0
    g250: GeomPoint X=-57.5 Y=-86 Z=0
    g251: GeomPoint X=-52 Y=-78.5 Z=0
    g252: ArcOfCircle CenterX=-53.5 CenterY=-78.5 CenterZ=0 NormalX=0 NormalY=0 NormalZ=1 AngleXU=0 Radius=1.5 StartAngle=3.14159 EndAngle=6.28319
    g253: LineSegment StartX=-66 StartY=-69.5 StartZ=0 EndX=-66 EndY=-78.5 EndZ=0
    g254: LineSegment StartX=-63 StartY=-69.5 StartZ=0 EndX=-63 EndY=-78.5 EndZ=0
    g255: ArcOfCircle CenterX=-64.5 CenterY=-69.5 CenterZ=0 NormalX=0 NormalY=0 NormalZ=1 AngleXU=0 Radius=1.5 StartAngle=-4.4e-15 EndAngle=3.14159
    g256: LineSegment StartX=-52 StartY=-69.5 StartZ=0 EndX=-52 EndY=-78.5 EndZ=0
    g257: LineSegment StartX=-55 StartY=-69.5 StartZ=0 EndX=-55 EndY=-78.5 EndZ=0
    g258: ArcOfCircle CenterX=-53.5 CenterY=-69.5 CenterZ=0 NormalX=0 NormalY=0 NormalZ=1 AngleXU=0 Radius=1.5 StartAngle=1.1e-15 EndAngle=3.14159
    g259: LineSegment StartX=-64.5 StartY=-69.5 StartZ=0 EndX=-43.681 EndY=-69.5 EndZ=0
    g260: LineSegment StartX=-70 StartY=-92 StartZ=0 EndX=-41.8037 EndY=-92 EndZ=0
    g261: LineSegment StartX=-53.7864 StartY=-101 StartZ=0 EndX=-42.1994 EndY=-101 EndZ=0
    g262: LineSegment StartX=-48.2864 StartY=-93.5 StartZ=0 EndX=-41.9836 EndY=-93.5 EndZ=0
    g263: ArcOfCircle CenterX=-70 CenterY=-92 CenterZ=0 NormalX=0 NormalY=0 NormalZ=1 AngleXU=0 Radius=1.5 StartAngle=4.4e-15 EndAngle=3.14159
    g264: ArcOfCircle CenterX=-70 CenterY=-101 CenterZ=0 NormalX=0 NormalY=0 NormalZ=1 AngleXU=0 Radius=1.5 StartAngle=3.14159 EndAngle=6.28319
    g265: LineSegment StartX=-71.5 StartY=-92 StartZ=0 EndX=-71.5 EndY=-101 EndZ=0
    g266: LineSegment StartX=-68.5 StartY=-92 StartZ=0 EndX=-68.5 EndY=-101 EndZ=0
    g267: GeomPoint X=-59 Y=-92 Z=0
    g268: GeomPoint X=-57.5 Y=-101 Z=0
    g269: GeomPoint X=-52 Y=-93.5 Z=0
    g270: ArcOfCircle CenterX=-53.5 CenterY=-93.5 CenterZ=0 NormalX=0 NormalY=0 NormalZ=1 AngleXU=0 Radius=1.5 StartAngle=3.14159 EndAngle=6.28319
    g271: LineSegment StartX=-52 StartY=-84.5 StartZ=0 EndX=-52 EndY=-93.5 EndZ=0
    g272: LineSegment StartX=-55 StartY=-84.5 StartZ=0 EndX=-55 EndY=-93.5 EndZ=0
    g273: ArcOfCircle CenterX=-53.5 CenterY=-84.5 CenterZ=0 NormalX=0 NormalY=0 NormalZ=1 AngleXU=0 Radius=1.5 StartAngle=-4.4e-15 EndAngle=3.14159
    g274: LineSegment StartX=-64.5 StartY=-84.5 StartZ=0 EndX=-43.0295 EndY=-84.5 EndZ=0
    g275: LineSegment StartX=-70 StartY=88 StartZ=0 EndX=-31.9181 EndY=88 EndZ=0
    g276: LineSegment StartX=-68.5184 StartY=79 StartZ=0 EndX=-33.995 EndY=79 EndZ=0
    g277: LineSegment StartX=-71.5 StartY=88 StartZ=0 EndX=-71.5 EndY=79 EndZ=0
    g278: ArcOfCircle CenterX=-70 CenterY=88 CenterZ=0 NormalX=0 NormalY=0 NormalZ=1 AngleXU=0 Radius=1.5 StartAngle=1.1e-15 EndAngle=3.14159
    g279: LineSegment StartX=-68.5 StartY=88 StartZ=0 EndX=-68.5 EndY=79 EndZ=0
    g280: ArcOfCircle CenterX=-70 CenterY=79 CenterZ=0 NormalX=0 NormalY=0 NormalZ=1 AngleXU=0 Radius=1.5 StartAngle=3.14159 EndAngle=6.28319
    g281: ArcOfCircle CenterX=-59 CenterY=86 CenterZ=0 NormalX=0 NormalY=0 NormalZ=1 AngleXU=0 Radius=1.5 StartAngle=-9e-16 EndAngle=3.14159
    g282: LineSegment StartX=-60.5 StartY=86 StartZ=0 EndX=-60.5 EndY=79 EndZ=0
    g283: LineSegment StartX=-57.5 StartY=86 StartZ=0 EndX=-57.5 EndY=79 EndZ=0
    g284: ArcOfCircle CenterX=-59 CenterY=79 CenterZ=0 NormalX=0 NormalY=0 NormalZ=1 AngleXU=0 Radius=1.5 StartAngle=3.14159 EndAngle=6.28319
    g285: ArcOfCircle CenterX=-59 CenterY=-77 CenterZ=0 NormalX=0 NormalY=0 NormalZ=1 AngleXU=0 Radius=1.5 StartAngle=2.1e-15 EndAngle=3.14159
    g286: LineSegment StartX=-60.5 StartY=-77 StartZ=0 EndX=-60.5 EndY=-84 EndZ=0
    g287: LineSegment StartX=-57.5 StartY=-77 StartZ=0 EndX=-57.5 EndY=-84 EndZ=0
    g288: ArcOfCircle CenterX=-59 CenterY=-84 CenterZ=0 NormalX=0 NormalY=0 NormalZ=1 AngleXU=0 Radius=1.5 StartAngle=3.14159 EndAngle=6.28319
  constraints (630):
    c: Horizontal(g0)
    c: Horizontal(g1)
    c: Horizontal(g2)
    c: Horizontal(g3)
    c: DistanceX(g0,g-1) = 70
    c: DistanceX(g2,g-1) = 64.5
    c: DistanceX(g1,g-1) = 68.5
    c: DistanceX(g3,g-1) = 63
    c: DistanceY(g1,g0) = 9
    c: DistanceY(g3,g2) = 9
    c: Tangent(g4,g7) = 1.5708
    c: Tangent(g4,g6) = -1.5708
    c: Tangent(g6,g5) = -1.5708
    c: Tangent(g7,g5) = 1.5708
    c: Vertical(g6)
    c: Equal(g4,g5)
    c: Coincident(g4,g0)
    c: PointOnObject(g5,g1)
    c: Tangent(g8,g11) = 1.5708
    c: Tangent(g8,g10) = -1.5708
    c: Tangent(g10,g9) = -1.5708
    c: Tangent(g11,g9) = 1.5708
    c: Vertical(g10)
    c: Equal(g8,g9)
    c: Coincident(g8,g2)
    c: PointOnObject(g9,g3)
    c: DistanceX(g4,g4) = 3
    c: DistanceX(g8,g8) = 3
    c: PointOnObject(g13,g2)
    c: PointOnObject(g14,g1)
    c: PointOnObject(g15,g3)
    c: DistanceX(g4,g12) = 11
    c: DistanceX(g8,g13) = 11
    c: DistanceX(g5,g14) = 11
    c: DistanceX(g9,g15) = 11
    c: PointOnObject(g12,g0)
    c: Tangent(g16,g19) = 1.5708
    c: Tangent(g16,g18) = -1.5708
    c: Tangent(g18,g17) = -1.5708
    c: Tangent(g19,g17) = 1.5708
    c: Vertical(g18)
    c: Equal(g16,g17)
    c: Coincident(g16,g12)
    c: Tangent(g20,g23) = 1.5708
    c: Tangent(g20,g22) = -1.5708
    c: Tangent(g22,g21) = -1.5708
    c: Tangent(g23,g21) = 1.5708
    c: Vertical(g22)
    c: Equal(g20,g21)
    c: Coincident(g17,g14)
    c: Coincident(g21,g15)
    c: Coincident(g20,g13)
    c: DistanceY(g3,g0) = 1.5
    c: Horizontal(g24)
    c: Horizontal(g25)
    c: Horizontal(g26)
    c: Horizontal(g27)
    c: DistanceY(g25,g24) = 9
    c: DistanceY(g27,g26) = 9
    c: Tangent(g28,g31) = 1.5708
    c: Tangent(g28,g30) = -1.5708
    c: Tangent(g30,g29) = -1.5708
    c: Tangent(g31,g29) = 1.5708
    c: Vertical(g30)
    c: Equal(g28,g29)
    c: Coincident(g28,g24)
    c: PointOnObject(g29,g25)
    c: Tangent(g32,g35) = 1.5708
    c: Tangent(g32,g34) = -1.5708
    c: Tangent(g34,g33) = -1.5708
    c: Tangent(g35,g33) = 1.5708
    c: Vertical(g34)
    c: Equal(g32,g33)
    c: Coincident(g32,g26)
    c: PointOnObject(g33,g27)
    c: Equal(g4,g28) = 3
    c: Equal(g8,g32) = 3
    c: PointOnObject(g37,g26)
    c: PointOnObject(g38,g25)
    c: PointOnObject(g39,g27)
    c: DistanceX(g28,g36) = 11
    c: DistanceX(g32,g37) = 11
    c: DistanceX(g29,g38) = 11
    c: DistanceX(g33,g39) = 11
    c: PointOnObject(g36,g24)
    c: Tangent(g40,g43) = 1.5708
    c: Tangent(g40,g42) = -1.5708
    c: Tangent(g42,g41) = -1.5708
    c: Tangent(g43,g41) = 1.5708
    c: Vertical(g42)
    c: Equal(g40,g41)
    c: Coincident(g40,g36)
    c: Tangent(g44,g47) = 1.5708
    c: Tangent(g44,g46) = -1.5708
    c: Tangent(g46,g45) = -1.5708
    c: Tangent(g47,g45) = 1.5708
    c: Vertical(g46)
    c: Equal(g44,g45)
    c: Coincident(g41,g38)
    c: Coincident(g45,g39)
    c: Coincident(g44,g37)
    c: DistanceY(g27,g24) = 1.5
    c: DistanceX(g28,g32) = 5.5
    c: Vertical(g28,g5)
    c: Horizontal(g48)
    c: Horizontal(g49)
    c: Horizontal(g50)
    c: Horizontal(g51)
    c: DistanceY(g49,g48) = 9
    c: DistanceY(g51,g50) = 9
    c: Tangent(g52,g55) = 1.5708
    c: Tangent(g52,g54) = -1.5708
    c: Tangent(g54,g53) = -1.5708
    c: Tangent(g55,g53) = 1.5708
    c: Vertical(g54)
    c: Equal(g52,g53)
    c: Coincident(g52,g48)
    c: PointOnObject(g53,g49)
    c: Tangent(g56,g59) = 1.5708
    c: Tangent(g56,g58) = -1.5708
    c: Tangent(g58,g57) = -1.5708
    c: Tangent(g59,g57) = 1.5708
    c: Vertical(g58)
    c: Equal(g56,g57)
    c: Coincident(g56,g50)
    c: PointOnObject(g57,g51)
    c: Equal(g4,g52) = 3
    c: Equal(g8,g56) = 3
    c: PointOnObject(g61,g50)
    c: PointOnObject(g62,g49)
    c: PointOnObject(g63,g51)
    c: DistanceX(g52,g60) = 11
    c: DistanceX(g56,g61) = 11
    c: DistanceX(g53,g62) = 11
    c: DistanceX(g57,g63) = 11
    c: PointOnObject(g60,g48)
    c: Tangent(g64,g67) = 1.5708
    c: Tangent(g64,g66) = -1.5708
    c: Tangent(g66,g65) = -1.5708
    c: Tangent(g67,g65) = 1.5708
    c: Vertical(g66)
    c: Equal(g64,g65)
    c: Coincident(g64,g60)
    c: Tangent(g68,g71) = 1.5708
    c: Tangent(g68,g70) = -1.5708
    c: Tangent(g70,g69) = -1.5708
    c: Tangent(g71,g69) = 1.5708
    c: Vertical(g70)
    c: Equal(g68,g69)
    c: Coincident(g65,g62)
    c: Coincident(g69,g63)
    c: Coincident(g68,g61)
    c: DistanceY(g51,g48) = 1.5
    c: Horizontal(g72)
    c: Horizontal(g73)
    c: Horizontal(g74)
    c: Horizontal(g75)
    c: DistanceY(g73,g72) = 9
    c: DistanceY(g75,g74) = 9
    c: Tangent(g76,g79) = 1.5708
    c: Tangent(g76,g78) = -1.5708
    c: Tangent(g78,g77) = -1.5708
    c: Tangent(g79,g77) = 1.5708
    c: Vertical(g78)
    c: Equal(g76,g77)
    c: Coincident(g76,g72)
    c: PointOnObject(g77,g73)
    c: Tangent(g80,g83) = 1.5708
    c: Tangent(g80,g82) = -1.5708
    c: Tangent(g82,g81) = -1.5708
    c: Tangent(g83,g81) = 1.5708
    c: Vertical(g82)
    c: Equal(g80,g81)
    c: Coincident(g80,g74)
    c: PointOnObject(g81,g75)
    c: Equal(g52,g76) = 3
    c: Equal(g56,g80) = 3
    c: PointOnObject(g85,g74)
    c: PointOnObject(g86,g73)
    c: PointOnObject(g87,g75)
    c: DistanceX(g76,g84) = 11
    c: DistanceX(g80,g85) = 11
    c: DistanceX(g77,g86) = 11
    c: DistanceX(g81,g87) = 11
    c: PointOnObject(g84,g72)
    c: Tangent(g88,g91) = 1.5708
    c: Tangent(g88,g90) = -1.5708
    c: Tangent(g90,g89) = -1.5708
    c: Tangent(g91,g89) = 1.5708
    c: Vertical(g90)
    c: Equal(g88,g89)
    c: Coincident(g88,g84)
    c: Tangent(g92,g95) = 1.5708
    c: Tangent(g92,g94) = -1.5708
    c: Tangent(g94,g93) = -1.5708
    c: Tangent(g95,g93) = 1.5708
    c: Vertical(g94)
    c: Equal(g92,g93)
    c: Coincident(g89,g86)
    c: Coincident(g93,g87)
    c: Coincident(g92,g85)
    c: DistanceY(g75,g72) = 1.5
    c: DistanceX(g76,g80) = 5.5
    c: Vertical(g76,g53)
    c: DistanceY(g74,g49) = -1.5
    c: DistanceY(g50,g25) = -1.5
    c: Vertical(g52,g29)
    c: Vertical(g57,g80)
    c: Horizontal(g96)
    c: Horizontal(g97)
    c: Horizontal(g98)
    c: Horizontal(g99)
    c: DistanceY(g97,g96) = 9
    c: DistanceY(g99,g98) = 9
    c: Tangent(g100,g103) = 1.5708
    c: Tangent(g100,g102) = -1.5708
    c: Tangent(g102,g101) = -1.5708
    c: Tangent(g103,g101) = 1.5708
    c: Vertical(g102)
    c: Equal(g100,g101)
    c: Coincident(g100,g96)
    c: PointOnObject(g101,g97)
    c: Tangent(g104,g107) = 1.5708
    c: Tangent(g104,g106) = -1.5708
    c: Tangent(g106,g105) = -1.5708
    c: Tangent(g107,g105) = 1.5708
    c: Vertical(g106)
    c: Equal(g104,g105)
    c: Coincident(g104,g98)
    c: PointOnObject(g105,g99)
    c: Equal(g4,g100) = 3
    c: Equal(g8,g104) = 3
    c: PointOnObject(g109,g98)
    c: PointOnObject(g110,g97)
    c: PointOnObject(g111,g99)
    c: DistanceX(g100,g108) = 11
    c: DistanceX(g104,g109) = 11
    c: DistanceX(g101,g110) = 11
    c: DistanceX(g105,g111) = 11
    c: PointOnObject(g108,g96)
    c: Tangent(g112,g115) = 1.5708
    c: Tangent(g112,g114) = -1.5708
    c: Tangent(g114,g113) = -1.5708
    c: Tangent(g115,g113) = 1.5708
    c: Vertical(g114)
    c: Equal(g112,g113)
    c: Coincident(g112,g108)
    c: Tangent(g116,g119) = 1.5708
    c: Tangent(g116,g118) = -1.5708
    c: Tangent(g118,g117) = -1.5708
    c: Tangent(g119,g117) = 1.5708
    c: Vertical(g118)
    c: Equal(g116,g117)
    c: Coincident(g113,g110)
    c: Coincident(g117,g111)
    c: Coincident(g116,g109)
    c: DistanceY(g99,g96) = 1.5
    c: Horizontal(g120)
    c: Horizontal(g121)
    c: Horizontal(g122)
    c: Horizontal(g123)
    c: DistanceY(g121,g120) = 9
    c: DistanceY(g123,g122) = 9
    c: Tangent(g124,g127) = 1.5708
    c: Tangent(g124,g126) = -1.5708
    c: Tangent(g126,g125) = -1.5708
    c: Tangent(g127,g125) = 1.5708
    c: Vertical(g126)
    c: Equal(g124,g125)
    c: Coincident(g124,g120)
    c: PointOnObject(g125,g121)
    c: Tangent(g128,g131) = 1.5708
    c: Tangent(g128,g130) = -1.5708
    c: Tangent(g130,g129) = -1.5708
    c: Tangent(g131,g129) = 1.5708
    c: Vertical(g130)
    c: Equal(g128,g129)
    c: Coincident(g128,g122)
    c: PointOnObject(g129,g123)
    c: Equal(g100,g124) = 3
    c: Equal(g104,g128) = 3
    c: PointOnObject(g133,g122)
    c: PointOnObject(g134,g121)
    c: PointOnObject(g135,g123)
    c: DistanceX(g124,g132) = 11
    c: DistanceX(g128,g133) = 11
    c: DistanceX(g125,g134) = 11
    c: DistanceX(g129,g135) = 11
    c: PointOnObject(g132,g120)
    c: Tangent(g136,g139) = 1.5708
    c: Tangent(g136,g138) = -1.5708
    c: Tangent(g138,g137) = -1.5708
    c: Tangent(g139,g137) = 1.5708
    c: Vertical(g138)
    c: Equal(g136,g137)
    c: Coincident(g136,g132)
    c: Tangent(g140,g143) = 1.5708
    c: Tangent(g140,g142) = -1.5708
    c: Tangent(g142,g141) = -1.5708
    c: Tangent(g143,g141) = 1.5708
    c: Vertical(g142)
    c: Equal(g140,g141)
    c: Coincident(g137,g134)
    c: Coincident(g141,g135)
    c: Coincident(g140,g133)
    c: DistanceY(g123,g120) = 1.5
    c: DistanceX(g124,g128) = 5.5
    c: Vertical(g124,g101)
    c: DistanceY(g122,g97) = -1.5
    c: Horizontal(g144)
    c: Horizontal(g145)
    c: Horizontal(g146)
    c: Horizontal(g147)
    c: DistanceY(g145,g144) = 9
    c: DistanceY(g147,g146) = 9
    c: Tangent(g148,g151) = 1.5708
    c: Tangent(g148,g150) = -1.5708
    c: Tangent(g150,g149) = -1.5708
    c: Tangent(g151,g149) = 1.5708
    c: Vertical(g150)
    c: Equal(g148,g149)
    c: Coincident(g148,g144)
    c: PointOnObject(g149,g145)
    c: Tangent(g152,g155) = 1.5708
    c: Tangent(g152,g154) = -1.5708
    c: Tangent(g154,g153) = -1.5708
    c: Tangent(g155,g153) = 1.5708
    c: Vertical(g154)
    c: Equal(g152,g153)
    c: Coincident(g152,g146)
    c: PointOnObject(g153,g147)
    c: Equal(g100,g148) = 3
    c: Equal(g104,g152) = 3
    c: PointOnObject(g157,g146)
    c: PointOnObject(g158,g145)
    c: PointOnObject(g159,g147)
    c: DistanceX(g148,g156) = 11
    c: DistanceX(g152,g157) = 11
    c: DistanceX(g149,g158) = 11
    c: DistanceX(g153,g159) = 11
    c: PointOnObject(g156,g144)
    c: Tangent(g160,g163) = 1.5708
    c: Tangent(g160,g162) = -1.5708
    c: Tangent(g162,g161) = -1.5708
    c: Tangent(g163,g161) = 1.5708
    c: Vertical(g162)
    c: Equal(g160,g161)
    c: Coincident(g160,g156)
    c: Tangent(g164,g167) = 1.5708
    c: Tangent(g164,g166) = -1.5708
    c: Tangent(g166,g165) = -1.5708
    c: Tangent(g167,g165) = 1.5708
    c: Vertical(g166)
    c: Equal(g164,g165)
    c: Coincident(g161,g158)
    c: Coincident(g165,g159)
    c: Coincident(g164,g157)
    c: DistanceY(g147,g144) = 1.5
    c: Horizontal(g168)
    c: Horizontal(g169)
    c: Horizontal(g170)
    c: Horizontal(g171)
    c: DistanceY(g169,g168) = 9
    c: DistanceY(g171,g170) = 9
    c: Tangent(g172,g175) = 1.5708
    c: Tangent(g172,g174) = -1.5708
    c: Tangent(g174,g173) = -1.5708
    c: Tangent(g175,g173) = 1.5708
    c: Vertical(g174)
    c: Equal(g172,g173)
    c: Coincident(g172,g168)
    c: PointOnObject(g173,g169)
    c: Tangent(g176,g179) = 1.5708
    c: Tangent(g176,g178) = -1.5708
    c: Tangent(g178,g177) = -1.5708
    c: Tangent(g179,g177) = 1.5708
    c: Vertical(g178)
    c: Equal(g176,g177)
    c: Coincident(g176,g170)
    c: PointOnObject(g177,g171)
    c: Equal(g148,g172) = 3
    c: Equal(g152,g176) = 3
    c: PointOnObject(g181,g170)
    c: PointOnObject(g182,g169)
    c: PointOnObject(g183,g171)
    c: DistanceX(g172,g180) = 11
    c: DistanceX(g176,g181) = 11
    c: DistanceX(g173,g182) = 11
    c: DistanceX(g177,g183) = 11
    c: PointOnObject(g180,g168)
    c: Tangent(g184,g187) = 1.5708
    c: Tangent(g184,g186) = -1.5708
    c: Tangent(g186,g185) = -1.5708
    c: Tangent(g187,g185) = 1.5708
    c: Vertical(g186)
    c: Equal(g184,g185)
    c: Coincident(g184,g180)
    c: Tangent(g188,g191) = 1.5708
    c: Tangent(g188,g190) = -1.5708
    c: Tangent(g190,g189) = -1.5708
    c: Tangent(g191,g189) = 1.5708
    c: Vertical(g190)
    c: Equal(g188,g189)
    c: Coincident(g185,g182)
    c: Coincident(g189,g183)
    c: Coincident(g188,g181)
    c: DistanceY(g171,g168) = 1.5
    c: DistanceX(g172,g176) = 5.5
    c: Vertical(g172,g149)
    c: DistanceY(g170,g145) = -1.5
    c: DistanceY(g146,g121) = -1.5
    c: Vertical(g148,g125)
    c: Vertical(g153,g176)
    c: Vertical(g117,g133)
    c: DistanceY(g98,g73) = -1.5
    c: Vertical(g77,g100)
    c: Horizontal(g193)
    c: Horizontal(g194)
    c: Horizontal(g195)
    c: Horizontal(g196)
    c: DistanceY(g194,g193) = 9
    c: DistanceY(g196,g195) = 9
    c: Tangent(g197,g200) = 1.5708
    c: Tangent(g197,g199) = -1.5708
    c: Tangent(g199,g198) = -1.5708
    c: Tangent(g200,g198) = 1.5708
    c: Vertical(g199)
    c: Equal(g197,g198)
    c: Coincident(g197,g193)
    c: PointOnObject(g198,g194)
    c: Tangent(g201,g204) = 1.5708
    c: Tangent(g201,g203) = -1.5708
    c: Tangent(g203,g202) = -1.5708
    c: Tangent(g204,g202) = 1.5708
    c: Vertical(g203)
    c: Equal(g201,g202)
    c: Coincident(g201,g195)
    c: PointOnObject(g202,g196)
    c: PointOnObject(g206,g195)
    c: PointOnObject(g207,g194)
    c: PointOnObject(g208,g196)
    c: DistanceX(g197,g205) = 11
    c: DistanceX(g201,g206) = 11
    c: DistanceX(g198,g207) = 11
    c: DistanceX(g202,g208) = 11
    c: PointOnObject(g205,g193)
    c: Tangent(g209,g212) = 1.5708
    c: Tangent(g209,g211) = -1.5708
    c: Tangent(g211,g210) = -1.5708
    c: Tangent(g212,g210) = 1.5708
    c: Vertical(g211)
    c: Equal(g209,g210)
    c: Coincident(g209,g205)
    c: Tangent(g213,g216) = 1.5708
    c: Tangent(g213,g215) = -1.5708
    c: Tangent(g215,g214) = -1.5708
    c: Tangent(g216,g214) = 1.5708
    c: Vertical(g215)
    c: Equal(g213,g214)
    c: Coincident(g210,g207)
    c: Coincident(g214,g208)
    c: Coincident(g213,g206)
    c: DistanceY(g196,g193) = 1.5
    c: Horizontal(g217)
    c: Horizontal(g218)
    c: Horizontal(g219)
    c: Horizontal(g220)
    c: DistanceY(g218,g217) = 9
    c: DistanceY(g220,g219) = 9
    c: Tangent(g221,g224) = 1.5708
    c: Tangent(g221,g223) = -1.5708
    c: Tangent(g223,g222) = -1.5708
    c: Tangent(g224,g222) = 1.5708
    c: Vertical(g223)
    c: Equal(g221,g222)
    c: Coincident(g221,g217)
    c: PointOnObject(g222,g218)
    c: Tangent(g225,g228) = 1.5708
    c: Tangent(g225,g227) = -1.5708
    c: Tangent(g227,g226) = -1.5708
    c: Tangent(g228,g226) = 1.5708
    c: Vertical(g227)
    c: Equal(g225,g226)
    c: Coincident(g225,g219)
    c: PointOnObject(g226,g220)
    c: Equal(g197,g221) = 3
    c: Equal(g201,g225) = 3
    c: PointOnObject(g230,g219)
    c: PointOnObject(g231,g218)
    c: PointOnObject(g232,g220)
    c: DistanceX(g221,g229) = 11
    c: DistanceX(g225,g230) = 11
    c: DistanceX(g222,g231) = 11
    c: DistanceX(g226,g232) = 11
    c: PointOnObject(g229,g217)
    c: Tangent(g233,g236) = 1.5708
    c: Tangent(g233,g235) = -1.5708
    c: Tangent(g235,g234) = -1.5708
    c: Tangent(g236,g234) = 1.5708
    c: Vertical(g235)
    c: Equal(g233,g234)
    c: Coincident(g233,g229)
    c: Tangent(g237,g240) = 1.5708
    c: Tangent(g237,g239) = -1.5708
    c: Tangent(g239,g238) = -1.5708
    c: Tangent(g240,g238) = 1.5708
    c: Vertical(g239)
    c: Equal(g237,g238)
    c: Coincident(g234,g231)
    c: Coincident(g238,g232)
    c: Coincident(g237,g230)
    c: DistanceY(g220,g217) = 1.5
    c: DistanceX(g221,g225) = 5.5
    c: Vertical(g221,g198)
    c: DistanceY(g219,g194) = -1.5
    c: Vertical(g202,g225)
    c: DistanceX(g197,g197) = 3
    c: DistanceX(g201,g201) = 3
    c: DistanceY(g195,g169) = -1.5
    c: Vertical(g197,g173)
    c: DistanceY(g1,g26) = 1.5
    c: Horizontal(g241)
    c: Horizontal(g259)
    c: Horizontal(g243)
    c: DistanceY(g242,g241) = 9
    c: DistanceY(g243,g259) = 9
    c: Tangent(g244,g247) = 1.5708
    c: Tangent(g244,g246) = -1.5708
    c: Tangent(g246,g245) = -1.5708
    c: Tangent(g247,g245) = 1.5708
    c: Vertical(g246)
    c: Equal(g244,g245)
    c: Coincident(g244,g241)
    c: PointOnObject(g245,g242)
    c: Tangent(g255,g254) = 1.5708
    c: Tangent(g255,g253) = -1.5708
    c: Tangent(g253,g248) = -1.5708
    c: Tangent(g254,g248) = 1.5708
    c: Vertical(g253)
    c: Equal(g255,g248)
    c: Coincident(g255,g259)
    c: PointOnObject(g248,g243)
    c: PointOnObject(g251,g243)
    c: DistanceX(g244,g249) = 11
    c: DistanceX(g245,g250) = 11
    c: DistanceX(g248,g251) = 11
    c: PointOnObject(g249,g241)
    c: Tangent(g258,g256) = 1.5708
    c: Tangent(g258,g257) = -1.5708
    c: Tangent(g257,g252) = -1.5708
    c: Tangent(g256,g252) = 1.5708
    c: Vertical(g257)
    c: Equal(g258,g252)
    c: Coincident(g252,g251)
    c: DistanceY(g243,g241) = 1.5
    c: DistanceX(g244,g255) = 5.5
    c: Vertical(g244,g222)
    c: DistanceX(g244,g244) = 3
    c: DistanceX(g253,g254) = 3
    c: DistanceY(g252,g258) = 9
    c: Horizontal(g260)
    c: Horizontal(g261)
    c: Horizontal(g274)
    c: Horizontal(g262)
    c: DistanceY(g261,g260) = 9
    c: DistanceY(g262,g274) = 9
    c: Tangent(g263,g266) = 1.5708
    c: Tangent(g263,g265) = -1.5708
    c: Tangent(g265,g264) = -1.5708
    c: Tangent(g266,g264) = 1.5708
    c: Vertical(g265)
    c: Equal(g263,g264)
    c: Coincident(g263,g260)
    c: PointOnObject(g264,g261)
    c: PointOnObject(g268,g261)
    c: PointOnObject(g269,g262)
    c: DistanceX(g263,g267) = 11
    c: DistanceX(g264,g268) = 11
    c: PointOnObject(g267,g260)
    c: Tangent(g273,g271) = 1.5708
    c: Tangent(g273,g272) = -1.5708
    c: Tangent(g272,g270) = -1.5708
    c: Tangent(g271,g270) = 1.5708
    c: Vertical(g272)
    c: Equal(g273,g270)
    c: Coincident(g270,g269)
    c: DistanceY(g262,g260) = 1.5
    c: Equal(g244,g263) = 3
    c: DistanceY(g270,g273) = 9
    c: DistanceX(g272,g271) = 3
    c: DistanceY(g274,g242) = -1.5
    c: DistanceY(g259,g218) = -1.5
    c: Horizontal(g275)
    c: Horizontal(g276)
    c: DistanceY(g276,g275) = 9
    c: Tangent(g278,g279) = 1.5708
    c: Tangent(g278,g277) = -1.5708
    c: Tangent(g277,g280) = -1.5708
    c: Tangent(g279,g280) = 1.5708
    c: Vertical(g277)
    c: Equal(g278,g280)
    c: Coincident(g278,g275)
    c: PointOnObject(g280,g276)
    c: Equal(g4,g278) = 3
    c: Vertical(g280,g4)
    c: DistanceY(g2,g276) = -1.5
    c: Tangent(g281,g283) = 1.5708
    c: Tangent(g281,g282) = -1.5708
    c: Tangent(g282,g284) = -1.5708
    c: Tangent(g283,g284) = 1.5708
    c: Vertical(g282)
    c: Equal(g281,g284)
    c: Horizontal(g284,g280)
    c: DistanceX(g282,g283) = 3
    c: DistanceX(g279,g283) = 11
    c: DistanceY(g284,g281) = 7
    c: DistanceY(g-1,g275) = 88
    c: DistanceX(g257,g256) = 3
    c: Horizontal(g242,g245)
    c: Tangent(g285,g287) = 1.5708
    c: Tangent(g285,g286) = -1.5708
    c: Tangent(g286,g288) = -1.5708
    c: Tangent(g287,g288) = 1.5708
    c: Vertical(g286)
    c: Equal(g285,g288)
    c: DistanceX(g286,g287) = 3
    c: DistanceY(g288,g285) = 7
    c: Vertical(g285,g234)
    c: Horizontal(g285,g244)
    c: Vertical(g245,g263)
FEATURE [Sketcher::SketchObject] Sketch010
  FullyConstrained = false
  MapMode = 5
  Placement = pos=(-1.0955e-12,2.25,0) rot=(0,0.707107,0.707107;3.14159rad)
  sketch-geometry (178):
    g0: LineSegment StartX=-48 StartY=-101 StartZ=0 EndX=53.55 EndY=-101 EndZ=0
    g1: LineSegment StartX=-51.3392 StartY=-92 StartZ=0 EndX=54.3773 EndY=-92 EndZ=0
    g2: ArcOfCircle CenterX=-48 CenterY=-101 CenterZ=0 NormalX=0 NormalY=0 NormalZ=1 AngleXU=0 Radius=1.5 StartAngle=3.14159 EndAngle=6.28319
    g3: ArcOfCircle CenterX=-48 CenterY=-92 CenterZ=0 NormalX=0 NormalY=0 NormalZ=1 AngleXU=0 Radius=1.5 StartAngle=2.5e-15 EndAngle=3.14159
    g4: LineSegment StartX=-46.5 StartY=-101 StartZ=0 EndX=-46.5 EndY=-92 EndZ=0
    g5: LineSegment StartX=-49.5 StartY=-101 StartZ=0 EndX=-49.5 EndY=-92 EndZ=0
    g6: ArcOfCircle CenterX=-37 CenterY=-101 CenterZ=0 NormalX=0 NormalY=0 NormalZ=1 AngleXU=0 Radius=1.5 StartAngle=3.14159 EndAngle=6.28319
    g7: ArcOfCircle CenterX=-37 CenterY=-92 CenterZ=0 NormalX=0 NormalY=0 NormalZ=1 AngleXU=0 Radius=1.5 StartAngle=1e-16 EndAngle=3.14159
    g8: LineSegment StartX=-35.5 StartY=-101 StartZ=0 EndX=-35.5 EndY=-92 EndZ=0
    g9: LineSegment StartX=-38.5 StartY=-101 StartZ=0 EndX=-38.5 EndY=-92 EndZ=0
    g10: ArcOfCircle CenterX=-26 CenterY=-101 CenterZ=0 NormalX=0 NormalY=0 NormalZ=1 AngleXU=0 Radius=1.5 StartAngle=3.14159 EndAngle=6.28319
    g11: ArcOfCircle CenterX=-26 CenterY=-92 CenterZ=0 NormalX=0 NormalY=0 NormalZ=1 AngleXU=0 Radius=1.5 StartAngle=2e-15 EndAngle=3.14159
    g12: LineSegment StartX=-24.5 StartY=-101 StartZ=0 EndX=-24.5 EndY=-92 EndZ=0
    g13: LineSegment StartX=-27.5 StartY=-101 StartZ=0 EndX=-27.5 EndY=-92 EndZ=0
    g14: ArcOfCircle CenterX=-15 CenterY=-101 CenterZ=0 NormalX=0 NormalY=0 NormalZ=1 AngleXU=0 Radius=1.5 StartAngle=3.14159 EndAngle=6.28319
    g15: ArcOfCircle CenterX=-15 CenterY=-92 CenterZ=0 NormalX=0 NormalY=0 NormalZ=1 AngleXU=0 Radius=1.5 StartAngle=-3.6e-15 EndAngle=3.14159
    g16: LineSegment StartX=-13.5 StartY=-101 StartZ=0 EndX=-13.5 EndY=-92 EndZ=0
    g17: LineSegment StartX=-16.5 StartY=-101 StartZ=0 EndX=-16.5 EndY=-92 EndZ=0
    g18: ArcOfCircle CenterX=-4 CenterY=-101 CenterZ=0 NormalX=0 NormalY=0 NormalZ=1 AngleXU=0 Radius=1.5 StartAngle=3.14159 EndAngle=6.28319
    g19: ArcOfCircle CenterX=-4 CenterY=-92 CenterZ=0 NormalX=0 NormalY=0 NormalZ=1 AngleXU=0 Radius=1.5 StartAngle=-9e-16 EndAngle=3.14159
    g20: LineSegment StartX=-2.5 StartY=-101 StartZ=0 EndX=-2.5 EndY=-92 EndZ=0
    g21: LineSegment StartX=-5.5 StartY=-101 StartZ=0 EndX=-5.5 EndY=-92 EndZ=0
    g22: ArcOfCircle CenterX=7 CenterY=-101 CenterZ=0 NormalX=0 NormalY=0 NormalZ=1 AngleXU=0 Radius=1.5 StartAngle=3.14159 EndAngle=6.28319
    g23: ArcOfCircle CenterX=7 CenterY=-92 CenterZ=0 NormalX=0 NormalY=0 NormalZ=1 AngleXU=0 Radius=1.5 StartAngle=-1.8e-15 EndAngle=3.14159
    g24: LineSegment StartX=8.5 StartY=-101 StartZ=0 EndX=8.5 EndY=-92 EndZ=0
    g25: LineSegment StartX=5.5 StartY=-101 StartZ=0 EndX=5.5 EndY=-92 EndZ=0
    g26: ArcOfCircle CenterX=18 CenterY=-101 CenterZ=0 NormalX=0 NormalY=0 NormalZ=1 AngleXU=0 Radius=1.5 StartAngle=3.14159 EndAngle=6.28319
    g27: ArcOfCircle CenterX=18 CenterY=-92 CenterZ=0 NormalX=0 NormalY=0 NormalZ=1 AngleXU=0 Radius=1.5 StartAngle=3.5e-15 EndAngle=3.14159
    g28: LineSegment StartX=19.5 StartY=-101 StartZ=0 EndX=19.5 EndY=-92 EndZ=0
    g29: LineSegment StartX=16.5 StartY=-101 StartZ=0 EndX=16.5 EndY=-92 EndZ=0
    g30: ArcOfCircle CenterX=29 CenterY=-101 CenterZ=0 NormalX=0 NormalY=0 NormalZ=1 AngleXU=0 Radius=1.5 StartAngle=3.14159 EndAngle=6.28319
    g31: ArcOfCircle CenterX=29 CenterY=-92 CenterZ=0 NormalX=0 NormalY=0 NormalZ=1 AngleXU=0 Radius=1.5 StartAngle=-1.8e-15 EndAngle=3.14159
    g32: LineSegment StartX=30.5 StartY=-101 StartZ=0 EndX=30.5 EndY=-92 EndZ=0
    g33: LineSegment StartX=27.5 StartY=-101 StartZ=0 EndX=27.5 EndY=-92 EndZ=0
    g34: ArcOfCircle CenterX=40 CenterY=-101 CenterZ=0 NormalX=0 NormalY=0 NormalZ=1 AngleXU=0 Radius=1.5 StartAngle=3.14159 EndAngle=6.28319
    g35: ArcOfCircle CenterX=40 CenterY=-92 CenterZ=0 NormalX=0 NormalY=0 NormalZ=1 AngleXU=0 Radius=1.5 StartAngle=2.7e-15 EndAngle=3.14159
    g36: LineSegment StartX=41.5 StartY=-101 StartZ=0 EndX=41.5 EndY=-92 EndZ=0
    g37: LineSegment StartX=38.5 StartY=-101 StartZ=0 EndX=38.5 EndY=-92 EndZ=0
    g38: LineSegment StartX=-48 StartY=-71 StartZ=0 EndX=52.2726 EndY=-71 EndZ=0
    g39: LineSegment StartX=-51.9499 StartY=-62 StartZ=0 EndX=62.5023 EndY=-62 EndZ=0
    g40: ArcOfCircle CenterX=-37 CenterY=-71 CenterZ=0 NormalX=0 NormalY=0 NormalZ=1 AngleXU=0 Radius=1.5 StartAngle=3.14159 EndAngle=6.28319
    g41: ArcOfCircle CenterX=-37 CenterY=-62 CenterZ=0 NormalX=0 NormalY=0 NormalZ=1 AngleXU=0 Radius=1.5 StartAngle=-1.8e-15 EndAngle=3.14159
    g42: LineSegment StartX=-35.5 StartY=-71 StartZ=0 EndX=-35.5 EndY=-62 EndZ=0
    g43: LineSegment StartX=-38.5 StartY=-71 StartZ=0 EndX=-38.5 EndY=-62 EndZ=0
    g44: ArcOfCircle CenterX=-26 CenterY=-71 CenterZ=0 NormalX=0 NormalY=0 NormalZ=1 AngleXU=0 Radius=1.5 StartAngle=3.14159 EndAngle=6.28319
    g45: ArcOfCircle CenterX=-26 CenterY=-62 CenterZ=0 NormalX=0 NormalY=0 NormalZ=1 AngleXU=0 Radius=1.5 StartAngle=1.8e-15 EndAngle=3.14159
    g46: LineSegment StartX=-24.5 StartY=-71 StartZ=0 EndX=-24.5 EndY=-62 EndZ=0
    g47: LineSegment StartX=-27.5 StartY=-71 StartZ=0 EndX=-27.5 EndY=-62 EndZ=0
    g48: ArcOfCircle CenterX=-15 CenterY=-71 CenterZ=0 NormalX=0 NormalY=0 NormalZ=1 AngleXU=0 Radius=1.5 StartAngle=3.14159 EndAngle=6.28319
    g49: ArcOfCircle CenterX=-15 CenterY=-62 CenterZ=0 NormalX=0 NormalY=0 NormalZ=1 AngleXU=0 Radius=1.5 StartAngle=1.9e-15 EndAngle=3.14159
    g50: LineSegment StartX=-13.5 StartY=-71 StartZ=0 EndX=-13.5 EndY=-62 EndZ=0
    g51: LineSegment StartX=-16.5 StartY=-71 StartZ=0 EndX=-16.5 EndY=-62 EndZ=0
    g52: ArcOfCircle CenterX=-4 CenterY=-71 CenterZ=0 NormalX=0 NormalY=0 NormalZ=1 AngleXU=0 Radius=1.5 StartAngle=3.14159 EndAngle=6.28319
    g53: ArcOfCircle CenterX=-4 CenterY=-62 CenterZ=0 NormalX=0 NormalY=0 NormalZ=1 AngleXU=0 Radius=1.5 StartAngle=-9e-16 EndAngle=3.14159
    g54: LineSegment StartX=-2.5 StartY=-71 StartZ=0 EndX=-2.5 EndY=-62 EndZ=0
    g55: LineSegment StartX=-5.5 StartY=-71 StartZ=0 EndX=-5.5 EndY=-62 EndZ=0
    g56: ArcOfCircle CenterX=7 CenterY=-71 CenterZ=0 NormalX=0 NormalY=0 NormalZ=1 AngleXU=0 Radius=1.5 StartAngle=3.14159 EndAngle=6.28319
    g57: ArcOfCircle CenterX=7 CenterY=-62 CenterZ=0 NormalX=0 NormalY=0 NormalZ=1 AngleXU=0 Radius=1.5 StartAngle=0 EndAngle=3.14159
    g58: LineSegment StartX=8.5 StartY=-71 StartZ=0 EndX=8.5 EndY=-62 EndZ=0
    g59: LineSegment StartX=5.5 StartY=-71 StartZ=0 EndX=5.5 EndY=-62 EndZ=0
    g60: ArcOfCircle CenterX=18 CenterY=-71 CenterZ=0 NormalX=0 NormalY=0 NormalZ=1 AngleXU=0 Radius=1.5 StartAngle=3.14159 EndAngle=6.28319
    g61: ArcOfCircle CenterX=18 CenterY=-62 CenterZ=0 NormalX=0 NormalY=0 NormalZ=1 AngleXU=0 Radius=1.5 StartAngle=-9e-16 EndAngle=3.14159
    g62: LineSegment StartX=19.5 StartY=-71 StartZ=0 EndX=19.5 EndY=-62 EndZ=0
    g63: LineSegment StartX=16.5 StartY=-71 StartZ=0 EndX=16.5 EndY=-62 EndZ=0
    g64: ArcOfCircle CenterX=29 CenterY=-71 CenterZ=0 NormalX=0 NormalY=0 NormalZ=1 AngleXU=0 Radius=1.5 StartAngle=3.14159 EndAngle=6.28319
    g65: ArcOfCircle CenterX=29 CenterY=-62 CenterZ=0 NormalX=0 NormalY=0 NormalZ=1 AngleXU=0 Radius=1.5 StartAngle=1.2e-15 EndAngle=3.14159
    g66: LineSegment StartX=30.5 StartY=-71 StartZ=0 EndX=30.5 EndY=-62 EndZ=0
    g67: LineSegment StartX=27.5 StartY=-71 StartZ=0 EndX=27.5 EndY=-62 EndZ=0
    g68: ArcOfCircle CenterX=40 CenterY=-71 CenterZ=0 NormalX=0 NormalY=0 NormalZ=1 AngleXU=0 Radius=1.5 StartAngle=3.14159 EndAngle=6.28319
    g69: ArcOfCircle CenterX=40 CenterY=-62 CenterZ=0 NormalX=0 NormalY=0 NormalZ=1 AngleXU=0 Radius=1.5 StartAngle=2e-16 EndAngle=3.14159
    g70: LineSegment StartX=41.5 StartY=-71 StartZ=0 EndX=41.5 EndY=-62 EndZ=0
    g71: LineSegment StartX=38.5 StartY=-71 StartZ=0 EndX=38.5 EndY=-62 EndZ=0
    g72: LineSegment StartX=-48 StartY=-86 StartZ=0 EndX=54.3847 EndY=-86 EndZ=0
    g73: LineSegment StartX=-50.5044 StartY=-77 StartZ=0 EndX=55.2121 EndY=-77 EndZ=0
    g74: ArcOfCircle CenterX=-48 CenterY=-86 CenterZ=0 NormalX=0 NormalY=0 NormalZ=1 AngleXU=0 Radius=1.5 StartAngle=3.14159 EndAngle=6.28319
    g75: ArcOfCircle CenterX=-48 CenterY=-77 CenterZ=0 NormalX=0 NormalY=0 NormalZ=1 AngleXU=0 Radius=1.5 StartAngle=-3.6e-15 EndAngle=3.14159
    g76: LineSegment StartX=-46.5 StartY=-86 StartZ=0 EndX=-46.5 EndY=-77 EndZ=0
    g77: LineSegment StartX=-49.5 StartY=-86 StartZ=0 EndX=-49.5 EndY=-77 EndZ=0
    g78: ArcOfCircle CenterX=-37 CenterY=-86 CenterZ=0 NormalX=0 NormalY=0 NormalZ=1 AngleXU=0 Radius=1.5 StartAngle=3.14159 EndAngle=6.28319
    g79: ArcOfCircle CenterX=-37 CenterY=-77 CenterZ=0 NormalX=0 NormalY=0 NormalZ=1 AngleXU=0 Radius=1.5 StartAngle=4.2e-15 EndAngle=3.14159
    g80: LineSegment StartX=-35.5 StartY=-86 StartZ=0 EndX=-35.5 EndY=-77 EndZ=0
    g81: LineSegment StartX=-38.5 StartY=-86 StartZ=0 EndX=-38.5 EndY=-77 EndZ=0
    g82: ArcOfCircle CenterX=-26 CenterY=-86 CenterZ=0 NormalX=0 NormalY=0 NormalZ=1 AngleXU=0 Radius=1.5 StartAngle=3.14159 EndAngle=6.28319
    g83: ArcOfCircle CenterX=-26 CenterY=-77 CenterZ=0 NormalX=0 NormalY=0 NormalZ=1 AngleXU=0 Radius=1.5 StartAngle=-3.6e-15 EndAngle=3.14159
    g84: LineSegment StartX=-24.5 StartY=-86 StartZ=0 EndX=-24.5 EndY=-77 EndZ=0
    g85: LineSegment StartX=-27.5 StartY=-86 StartZ=0 EndX=-27.5 EndY=-77 EndZ=0
    g86: ArcOfCircle CenterX=-15 CenterY=-86 CenterZ=0 NormalX=0 NormalY=0 NormalZ=1 AngleXU=0 Radius=1.5 StartAngle=3.14159 EndAngle=6.28319
    g87: ArcOfCircle CenterX=-15 CenterY=-77 CenterZ=0 NormalX=0 NormalY=0 NormalZ=1 AngleXU=0 Radius=1.5 StartAngle=-1.8e-15 EndAngle=3.14159
    g88: LineSegment StartX=-13.5 StartY=-86 StartZ=0 EndX=-13.5 EndY=-77 EndZ=0
    g89: LineSegment StartX=-16.5 StartY=-86 StartZ=0 EndX=-16.5 EndY=-77 EndZ=0
    g90: ArcOfCircle CenterX=-4 CenterY=-86 CenterZ=0 NormalX=0 NormalY=0 NormalZ=1 AngleXU=0 Radius=1.5 StartAngle=3.14159 EndAngle=6.28319
    g91: ArcOfCircle CenterX=-4 CenterY=-77 CenterZ=0 NormalX=0 NormalY=0 NormalZ=1 AngleXU=0 Radius=1.5 StartAngle=-2.7e-15 EndAngle=3.14159
    g92: LineSegment StartX=-2.5 StartY=-86 StartZ=0 EndX=-2.5 EndY=-77 EndZ=0
    g93: LineSegment StartX=-5.5 StartY=-86 StartZ=0 EndX=-5.5 EndY=-77 EndZ=0
    g94: ArcOfCircle CenterX=7 CenterY=-86 CenterZ=0 NormalX=0 NormalY=0 NormalZ=1 AngleXU=0 Radius=1.5 StartAngle=3.14159 EndAngle=6.28319
    g95: ArcOfCircle CenterX=7 CenterY=-77 CenterZ=0 NormalX=0 NormalY=0 NormalZ=1 AngleXU=0 Radius=1.5 StartAngle=3.5e-15 EndAngle=3.14159
    g96: LineSegment StartX=8.5 StartY=-86 StartZ=0 EndX=8.5 EndY=-77 EndZ=0
    g97: LineSegment StartX=5.5 StartY=-86 StartZ=0 EndX=5.5 EndY=-77 EndZ=0
    g98: ArcOfCircle CenterX=18 CenterY=-86 CenterZ=0 NormalX=0 NormalY=0 NormalZ=1 AngleXU=0 Radius=1.5 StartAngle=3.14159 EndAngle=6.28319
    g99: ArcOfCircle CenterX=18 CenterY=-77 CenterZ=0 NormalX=0 NormalY=0 NormalZ=1 AngleXU=0 Radius=1.5 StartAngle=-1.8e-15 EndAngle=3.14159
    g100: LineSegment StartX=19.5 StartY=-86 StartZ=0 EndX=19.5 EndY=-77 EndZ=0
    g101: LineSegment StartX=16.5 StartY=-86 StartZ=0 EndX=16.5 EndY=-77 EndZ=0
    g102: ArcOfCircle CenterX=29 CenterY=-86 CenterZ=0 NormalX=0 NormalY=0 NormalZ=1 AngleXU=0 Radius=1.5 StartAngle=3.14159 EndAngle=6.28319
    g103: ArcOfCircle CenterX=29 CenterY=-77 CenterZ=0 NormalX=0 NormalY=0 NormalZ=1 AngleXU=0 Radius=1.5 StartAngle=-9e-16 EndAngle=3.14159
    g104: LineSegment StartX=30.5 StartY=-86 StartZ=0 EndX=30.5 EndY=-77 EndZ=0
    g105: LineSegment StartX=27.5 StartY=-86 StartZ=0 EndX=27.5 EndY=-77 EndZ=0
    g106: ArcOfCircle CenterX=40 CenterY=-86 CenterZ=0 NormalX=0 NormalY=0 NormalZ=1 AngleXU=0 Radius=1.5 StartAngle=3.14159 EndAngle=6.28319
    g107: ArcOfCircle CenterX=40 CenterY=-77 CenterZ=0 NormalX=0 NormalY=0 NormalZ=1 AngleXU=0 Radius=1.5 StartAngle=4.2e-15 EndAngle=3.14159
    g108: LineSegment StartX=41.5 StartY=-86 StartZ=0 EndX=41.5 EndY=-77 EndZ=0
    g109: LineSegment StartX=38.5 StartY=-86 StartZ=0 EndX=38.5 EndY=-77 EndZ=0
    g110: LineSegment StartX=-42.5 StartY=-93.5 StartZ=0 EndX=56.6539 EndY=-93.5 EndZ=0
    g111: LineSegment StartX=-48.2352 StartY=-84.5 StartZ=0 EndX=57.4813 EndY=-84.5 EndZ=0
    g112: ArcOfCircle CenterX=-42.5 CenterY=-93.5 CenterZ=0 NormalX=0 NormalY=0 NormalZ=1 AngleXU=0 Radius=1.5 StartAngle=3.14159 EndAngle=6.28319
    g113: ArcOfCircle CenterX=-42.5 CenterY=-84.5 CenterZ=0 NormalX=0 NormalY=0 NormalZ=1 AngleXU=0 Radius=1.5 StartAngle=2e-16 EndAngle=3.14159
    g114: LineSegment StartX=-41 StartY=-93.5 StartZ=0 EndX=-41 EndY=-84.5 EndZ=0
    g115: LineSegment StartX=-44 StartY=-93.5 StartZ=0 EndX=-44 EndY=-84.5 EndZ=0
    g116: ArcOfCircle CenterX=-31.5 CenterY=-93.5 CenterZ=0 NormalX=0 NormalY=0 NormalZ=1 AngleXU=0 Radius=1.5 StartAngle=3.14159 EndAngle=6.28319
    g117: ArcOfCircle CenterX=-31.5 CenterY=-84.5 CenterZ=0 NormalX=0 NormalY=0 NormalZ=1 AngleXU=0 Radius=1.5 StartAngle=0 EndAngle=3.14159
    g118: LineSegment StartX=-30 StartY=-93.5 StartZ=0 EndX=-30 EndY=-84.5 EndZ=0
    g119: LineSegment StartX=-33 StartY=-93.5 StartZ=0 EndX=-33 EndY=-84.5 EndZ=0
    g120: ArcOfCircle CenterX=-20.5 CenterY=-93.5 CenterZ=0 NormalX=0 NormalY=0 NormalZ=1 AngleXU=0 Radius=1.5 StartAngle=3.14159 EndAngle=6.28319
    g121: ArcOfCircle CenterX=-20.5 CenterY=-84.5 CenterZ=0 NormalX=0 NormalY=0 NormalZ=1 AngleXU=0 Radius=1.5 StartAngle=3.9e-15 EndAngle=3.14159
    g122: LineSegment StartX=-19 StartY=-93.5 StartZ=0 EndX=-19 EndY=-84.5 EndZ=0
    g123: LineSegment StartX=-22 StartY=-93.5 StartZ=0 EndX=-22 EndY=-84.5 EndZ=0
    g124: ArcOfCircle CenterX=-9.5 CenterY=-93.5 CenterZ=0 NormalX=0 NormalY=0 NormalZ=1 AngleXU=0 Radius=1.5 StartAngle=3.14159 EndAngle=6.28319
    g125: ArcOfCircle CenterX=-9.5 CenterY=-84.5 CenterZ=0 NormalX=0 NormalY=0 NormalZ=1 AngleXU=0 Radius=1.5 StartAngle=5e-16 EndAngle=3.14159
    g126: LineSegment StartX=-8 StartY=-93.5 StartZ=0 EndX=-8 EndY=-84.5 EndZ=0
    g127: LineSegment StartX=-11 StartY=-93.5 StartZ=0 EndX=-11 EndY=-84.5 EndZ=0
    g128: ArcOfCircle CenterX=1.5 CenterY=-93.5 CenterZ=0 NormalX=0 NormalY=0 NormalZ=1 AngleXU=0 Radius=1.5 StartAngle=3.14159 EndAngle=6.28319
    g129: ArcOfCircle CenterX=1.5 CenterY=-84.5 CenterZ=0 NormalX=0 NormalY=0 NormalZ=1 AngleXU=0 Radius=1.5 StartAngle=-1.8e-15 EndAngle=3.14159
    g130: LineSegment StartX=3 StartY=-93.5 StartZ=0 EndX=3 EndY=-84.5 EndZ=0
    g131: LineSegment StartX=6.74105e-11 StartY=-93.5 StartZ=0 EndX=6.74105e-11 EndY=-84.5 EndZ=0
    g132: ArcOfCircle CenterX=12.5 CenterY=-93.5 CenterZ=0 NormalX=0 NormalY=0 NormalZ=1 AngleXU=0 Radius=1.5 StartAngle=3.14159 EndAngle=6.28319
    g133: ArcOfCircle CenterX=12.5 CenterY=-84.5 CenterZ=0 NormalX=0 NormalY=0 NormalZ=1 AngleXU=0 Radius=1.5 StartAngle=3.1e-15 EndAngle=3.14159
    g134: LineSegment StartX=14 StartY=-93.5 StartZ=0 EndX=14 EndY=-84.5 EndZ=0
    g135: LineSegment StartX=11 StartY=-93.5 StartZ=0 EndX=11 EndY=-84.5 EndZ=0
    g136: ArcOfCircle CenterX=23.5 CenterY=-93.5 CenterZ=0 NormalX=0 NormalY=0 NormalZ=1 AngleXU=0 Radius=1.5 StartAngle=3.14159 EndAngle=6.28319
    g137: ArcOfCircle CenterX=23.5 CenterY=-84.5 CenterZ=0 NormalX=0 NormalY=0 NormalZ=1 AngleXU=0 Radius=1.5 StartAngle=8e-16 EndAngle=3.14159
    g138: LineSegment StartX=25 StartY=-93.5 StartZ=0 EndX=25 EndY=-84.5 EndZ=0
    g139: LineSegment StartX=22 StartY=-93.5 StartZ=0 EndX=22 EndY=-84.5 EndZ=0
    g140: ArcOfCircle CenterX=34.5 CenterY=-93.5 CenterZ=0 NormalX=0 NormalY=0 NormalZ=1 AngleXU=0 Radius=1.5 StartAngle=3.14159 EndAngle=6.28319
    g141: ArcOfCircle CenterX=34.5 CenterY=-84.5 CenterZ=0 NormalX=0 NormalY=0 NormalZ=1 AngleXU=0 Radius=1.5 StartAngle=1e-15 EndAngle=3.14159
    g142: LineSegment StartX=36 StartY=-93.5 StartZ=0 EndX=36 EndY=-84.5 EndZ=0
    g143: LineSegment StartX=33 StartY=-93.5 StartZ=0 EndX=33 EndY=-84.5 EndZ=0
    g144: LineSegment StartX=-42.5 StartY=-78.5 StartZ=0 EndX=51.8208 EndY=-78.5 EndZ=0
    g145: LineSegment StartX=-54.0617 StartY=-69.5 StartZ=0 EndX=51.6548 EndY=-69.5 EndZ=0
    g146: ArcOfCircle CenterX=-42.5 CenterY=-78.5 CenterZ=0 NormalX=0 NormalY=0 NormalZ=1 AngleXU=0 Radius=1.5 StartAngle=3.14159 EndAngle=6.28319
    g147: ArcOfCircle CenterX=-42.5 CenterY=-69.5 CenterZ=0 NormalX=0 NormalY=0 NormalZ=1 AngleXU=0 Radius=1.5 StartAngle=0 EndAngle=3.14159
    g148: LineSegment StartX=-41 StartY=-78.5 StartZ=0 EndX=-41 EndY=-69.5 EndZ=0
    g149: LineSegment StartX=-44 StartY=-78.5 StartZ=0 EndX=-44 EndY=-69.5 EndZ=0
    g150: ArcOfCircle CenterX=-31.5 CenterY=-78.5 CenterZ=0 NormalX=0 NormalY=0 NormalZ=1 AngleXU=0 Radius=1.5 StartAngle=3.14159 EndAngle=6.28319
    g151: ArcOfCircle CenterX=-31.5 CenterY=-69.5 CenterZ=0 NormalX=0 NormalY=0 NormalZ=1 AngleXU=0 Radius=1.5 StartAngle=-2.7e-15 EndAngle=3.14159
    g152: LineSegment StartX=-30 StartY=-78.5 StartZ=0 EndX=-30 EndY=-69.5 EndZ=0
    g153: LineSegment StartX=-33 StartY=-78.5 StartZ=0 EndX=-33 EndY=-69.5 EndZ=0
    g154: ArcOfCircle CenterX=-20.5 CenterY=-78.5 CenterZ=0 NormalX=0 NormalY=0 NormalZ=1 AngleXU=0 Radius=1.5 StartAngle=3.14159 EndAngle=6.28319
    g155: ArcOfCircle CenterX=-20.5 CenterY=-69.5 CenterZ=0 NormalX=0 NormalY=0 NormalZ=1 AngleXU=0 Radius=1.5 StartAngle=3.1e-15 EndAngle=3.14159
    g156: LineSegment StartX=-19 StartY=-78.5 StartZ=0 EndX=-19 EndY=-69.5 EndZ=0
    g157: LineSegment StartX=-22 StartY=-78.5 StartZ=0 EndX=-22 EndY=-69.5 EndZ=0
    g158: ArcOfCircle CenterX=-9.5 CenterY=-78.5 CenterZ=0 NormalX=0 NormalY=0 NormalZ=1 AngleXU=0 Radius=1.5 StartAngle=3.14159 EndAngle=6.28319
    g159: ArcOfCircle CenterX=-9.5 CenterY=-69.5 CenterZ=0 NormalX=0 NormalY=0 NormalZ=1 AngleXU=0 Radius=1.5 StartAngle=-3.6e-15 EndAngle=3.14159
    g160: LineSegment StartX=-8 StartY=-78.5 StartZ=0 EndX=-8 EndY=-69.5 EndZ=0
    g161: LineSegment StartX=-11 StartY=-78.5 StartZ=0 EndX=-11 EndY=-69.5 EndZ=0
    g162: ArcOfCircle CenterX=1.5 CenterY=-78.5 CenterZ=0 NormalX=0 NormalY=0 NormalZ=1 AngleXU=0 Radius=1.5 StartAngle=3.14159 EndAngle=6.28319
    g163: ArcOfCircle CenterX=1.5 CenterY=-69.5 CenterZ=0 NormalX=0 NormalY=0 NormalZ=1 AngleXU=0 Radius=1.5 StartAngle=4.5e-15 EndAngle=3.14159
    g164: LineSegment StartX=3 StartY=-78.5 StartZ=0 EndX=3 EndY=-69.5 EndZ=0
    g165: LineSegment StartX=2.08003e-11 StartY=-78.5 StartZ=0 EndX=2.08003e-11 EndY=-69.5 EndZ=0
    g166: ArcOfCircle CenterX=12.5 CenterY=-78.5 CenterZ=0 NormalX=0 NormalY=0 NormalZ=1 AngleXU=0 Radius=1.5 StartAngle=3.14159 EndAngle=6.28319
    g167: ArcOfCircle CenterX=12.5 CenterY=-69.5 CenterZ=0 NormalX=0 NormalY=0 NormalZ=1 AngleXU=0 Radius=1.5 StartAngle=3e-15 EndAngle=3.14159
    g168: LineSegment StartX=14 StartY=-78.5 StartZ=0 EndX=14 EndY=-69.5 EndZ=0
    g169: LineSegment StartX=11 StartY=-78.5 StartZ=0 EndX=11 EndY=-69.5 EndZ=0
    g170: ArcOfCircle CenterX=23.5 CenterY=-78.5 CenterZ=0 NormalX=0 NormalY=0 NormalZ=1 AngleXU=0 Radius=1.5 StartAngle=3.14159 EndAngle=6.28319
    g171: ArcOfCircle CenterX=23.5 CenterY=-69.5 CenterZ=0 NormalX=0 NormalY=0 NormalZ=1 AngleXU=0 Radius=1.5 StartAngle=4.7e-15 EndAngle=3.14159
    g172: LineSegment StartX=25 StartY=-78.5 StartZ=0 EndX=25 EndY=-69.5 EndZ=0
    g173: LineSegment StartX=22 StartY=-78.5 StartZ=0 EndX=22 EndY=-69.5 EndZ=0
    g174: ArcOfCircle CenterX=34.5 CenterY=-78.5 CenterZ=0 NormalX=0 NormalY=0 NormalZ=1 AngleXU=0 Radius=1.5 StartAngle=3.14159 EndAngle=6.28319
    g175: ArcOfCircle CenterX=34.5 CenterY=-69.5 CenterZ=0 NormalX=0 NormalY=0 NormalZ=1 AngleXU=0 Radius=1.5 StartAngle=-3.6e-15 EndAngle=3.14159
    g176: LineSegment StartX=36 StartY=-78.5 StartZ=0 EndX=36 EndY=-69.5 EndZ=0
    g177: LineSegment StartX=33 StartY=-78.5 StartZ=0 EndX=33 EndY=-69.5 EndZ=0
  constraints (435):
    c: Horizontal(g0)
    c: Horizontal(g1)
    c: DistanceY(g0,g1) = 9
    c: Tangent(g2,g5) = 1.5708
    c: Tangent(g2,g4) = -1.5708
    c: Tangent(g4,g3) = -1.5708
    c: Tangent(g5,g3) = 1.5708
    c: Vertical(g4)
    c: Equal(g2,g3)
    c: Coincident(g2,g0)
    c: DistanceX(g2,g2) = 3
    c: PointOnObject(g3,g1)
    c: Tangent(g6,g9) = 1.5708
    c: Tangent(g6,g8) = -1.5708
    c: Tangent(g8,g7) = -1.5708
    c: Tangent(g9,g7) = 1.5708
    c: Vertical(g8)
    c: Equal(g6,g7)
    c: Equal(g2,g6) = 3
    c: DistanceX(g2,g6) = 11
    c: Horizontal(g6,g2)
    c: Tangent(g10,g13) = 1.5708
    c: Tangent(g10,g12) = -1.5708
    c: Tangent(g12,g11) = -1.5708
    c: Tangent(g13,g11) = 1.5708
    c: Vertical(g12)
    c: Equal(g10,g11)
    c: Equal(g2,g10) = 3
    c: Tangent(g14,g17) = 1.5708
    c: Tangent(g14,g16) = -1.5708
    c: Tangent(g16,g15) = -1.5708
    c: Tangent(g17,g15) = 1.5708
    c: Vertical(g16)
    c: Equal(g14,g15)
    c: Equal(g10,g14) = 3
    c: DistanceX(g10,g14) = 11
    c: Horizontal(g14,g10)
    c: DistanceX(g6,g10) = 11
    c: Horizontal(g10,g6)
    c: Horizontal(g3,g7)
    c: Horizontal(g7,g11)
    c: Horizontal(g11,g15)
    c: Tangent(g18,g21) = 1.5708
    c: Tangent(g18,g20) = -1.5708
    c: Tangent(g20,g19) = -1.5708
    c: Tangent(g21,g19) = 1.5708
    c: Vertical(g20)
    c: Equal(g18,g19)
    c: Equal(g2,g18) = 3
    c: Tangent(g22,g25) = 1.5708
    c: Tangent(g22,g24) = -1.5708
    c: Tangent(g24,g23) = -1.5708
    c: Tangent(g25,g23) = 1.5708
    c: Vertical(g24)
    c: Equal(g22,g23)
    c: Equal(g18,g22) = 3
    c: DistanceX(g18,g22) = 11
    c: Horizontal(g22,g18)
    c: Tangent(g26,g29) = 1.5708
    c: Tangent(g26,g28) = -1.5708
    c: Tangent(g28,g27) = -1.5708
    c: Tangent(g29,g27) = 1.5708
    c: Vertical(g28)
    c: Equal(g26,g27)
    c: Equal(g18,g26) = 3
    c: Tangent(g30,g33) = 1.5708
    c: Tangent(g30,g32) = -1.5708
    c: Tangent(g32,g31) = -1.5708
    c: Tangent(g33,g31) = 1.5708
    c: Vertical(g32)
    c: Equal(g30,g31)
    c: Equal(g26,g30) = 3
    c: DistanceX(g26,g30) = 11
    c: Horizontal(g30,g26)
    c: DistanceX(g22,g26) = 11
    c: Horizontal(g26,g22)
    c: Horizontal(g19,g23)
    c: Horizontal(g23,g27)
    c: Horizontal(g27,g31)
    c: DistanceX(g14,g18) = 11
    c: Horizontal(g18,g14)
    c: Horizontal(g19,g15)
    c: Tangent(g34,g37) = 1.5708
    c: Tangent(g34,g36) = -1.5708
    c: Tangent(g36,g35) = -1.5708
    c: Tangent(g37,g35) = 1.5708
    c: Vertical(g36)
    c: Equal(g34,g35)
    c: DistanceX(g30,g34) = 11
    c: Horizontal(g30,g34)
    c: Horizontal(g31,g35)
    c: DistanceX(g34,g34) = 3
    c: Horizontal(g38)
    c: Horizontal(g39)
    c: DistanceY(g38,g39) = 9
    c: Tangent(g40,g43) = 1.5708
    c: Tangent(g40,g42) = -1.5708
    c: Tangent(g42,g41) = -1.5708
    c: Tangent(g43,g41) = 1.5708
    c: Vertical(g42)
    c: Equal(g40,g41)
    c: Tangent(g44,g47) = 1.5708
    c: Tangent(g44,g46) = -1.5708
    c: Tangent(g46,g45) = -1.5708
    c: Tangent(g47,g45) = 1.5708
    c: Vertical(g46)
    c: Equal(g44,g45)
    c: Tangent(g48,g51) = 1.5708
    c: Tangent(g48,g50) = -1.5708
    c: Tangent(g50,g49) = -1.5708
    c: Tangent(g51,g49) = 1.5708
    c: Vertical(g50)
    c: Equal(g48,g49)
    c: Equal(g44,g48) = 3
    c: DistanceX(g44,g48) = 11
    c: Horizontal(g48,g44)
    c: DistanceX(g40,g44) = 11
    c: Horizontal(g44,g40)
    c: Horizontal(g41,g45)
    c: Horizontal(g45,g49)
    c: Tangent(g52,g55) = 1.5708
    c: Tangent(g52,g54) = -1.5708
    c: Tangent(g54,g53) = -1.5708
    c: Tangent(g55,g53) = 1.5708
    c: Vertical(g54)
    c: Equal(g52,g53)
    c: Tangent(g56,g59) = 1.5708
    c: Tangent(g56,g58) = -1.5708
    c: Tangent(g58,g57) = -1.5708
    c: Tangent(g59,g57) = 1.5708
    c: Vertical(g58)
    c: Equal(g56,g57)
    c: Equal(g52,g56) = 3
    c: DistanceX(g52,g56) = 11
    c: Horizontal(g56,g52)
    c: Tangent(g60,g63) = 1.5708
    c: Tangent(g60,g62) = -1.5708
    c: Tangent(g62,g61) = -1.5708
    c: Tangent(g63,g61) = 1.5708
    c: Vertical(g62)
    c: Equal(g60,g61)
    c: Equal(g52,g60) = 3
    c: Tangent(g64,g67) = 1.5708
    c: Tangent(g64,g66) = -1.5708
    c: Tangent(g66,g65) = -1.5708
    c: Tangent(g67,g65) = 1.5708
    c: Vertical(g66)
    c: Equal(g64,g65)
    c: Equal(g60,g64) = 3
    c: DistanceX(g60,g64) = 11
    c: Horizontal(g64,g60)
    c: DistanceX(g56,g60) = 11
    c: Horizontal(g60,g56)
    c: Horizontal(g53,g57)
    c: Horizontal(g57,g61)
    c: Horizontal(g61,g65)
    c: DistanceX(g48,g52) = 11
    c: Horizontal(g52,g48)
    c: Horizontal(g53,g49)
    c: Tangent(g68,g71) = 1.5708
    c: Tangent(g68,g70) = -1.5708
    c: Tangent(g70,g69) = -1.5708
    c: Tangent(g71,g69) = 1.5708
    c: Vertical(g70)
    c: Equal(g68,g69)
    c: DistanceX(g64,g68) = 11
    c: Horizontal(g64,g68)
    c: Horizontal(g65,g69)
    c: Equal(g34,g68) = 3
    c: Horizontal(g72)
    c: Horizontal(g73)
    c: DistanceY(g72,g73) = 9
    c: Tangent(g74,g77) = 1.5708
    c: Tangent(g74,g76) = -1.5708
    c: Tangent(g76,g75) = -1.5708
    c: Tangent(g77,g75) = 1.5708
    c: Vertical(g76)
    c: Equal(g74,g75)
    c: Coincident(g74,g72)
    c: Equal(g2,g74) = 3
    c: PointOnObject(g75,g73)
    c: Tangent(g78,g81) = 1.5708
    c: Tangent(g78,g80) = -1.5708
    c: Tangent(g80,g79) = -1.5708
    c: Tangent(g81,g79) = 1.5708
    c: Vertical(g80)
    c: Equal(g78,g79)
    c: Equal(g74,g78) = 3
    c: DistanceX(g74,g78) = 11
    c: Horizontal(g78,g74)
    c: Tangent(g82,g85) = 1.5708
    c: Tangent(g82,g84) = -1.5708
    c: Tangent(g84,g83) = -1.5708
    c: Tangent(g85,g83) = 1.5708
    c: Vertical(g84)
    c: Equal(g82,g83)
    c: Equal(g74,g82) = 3
    c: Tangent(g86,g89) = 1.5708
    c: Tangent(g86,g88) = -1.5708
    c: Tangent(g88,g87) = -1.5708
    c: Tangent(g89,g87) = 1.5708
    c: Vertical(g88)
    c: Equal(g86,g87)
    c: Equal(g82,g86) = 3
    c: DistanceX(g82,g86) = 11
    c: Horizontal(g86,g82)
    c: DistanceX(g78,g82) = 11
    c: Horizontal(g82,g78)
    c: Horizontal(g75,g79)
    c: Horizontal(g79,g83)
    c: Horizontal(g83,g87)
    c: Tangent(g90,g93) = 1.5708
    c: Tangent(g90,g92) = -1.5708
    c: Tangent(g92,g91) = -1.5708
    c: Tangent(g93,g91) = 1.5708
    c: Vertical(g92)
    c: Equal(g90,g91)
    c: Equal(g74,g90) = 3
    c: Tangent(g94,g97) = 1.5708
    c: Tangent(g94,g96) = -1.5708
    c: Tangent(g96,g95) = -1.5708
    c: Tangent(g97,g95) = 1.5708
    c: Vertical(g96)
    c: Equal(g94,g95)
    c: Equal(g90,g94) = 3
    c: DistanceX(g90,g94) = 11
    c: Horizontal(g94,g90)
    c: Tangent(g98,g101) = 1.5708
    c: Tangent(g98,g100) = -1.5708
    c: Tangent(g100,g99) = -1.5708
    c: Tangent(g101,g99) = 1.5708
    c: Vertical(g100)
    c: Equal(g98,g99)
    c: Equal(g90,g98) = 3
    c: Tangent(g102,g105) = 1.5708
    c: Tangent(g102,g104) = -1.5708
    c: Tangent(g104,g103) = -1.5708
    c: Tangent(g105,g103) = 1.5708
    c: Vertical(g104)
    c: Equal(g102,g103)
    c: Equal(g98,g102) = 3
    c: DistanceX(g98,g102) = 11
    c: Horizontal(g102,g98)
    c: DistanceX(g94,g98) = 11
    c: Horizontal(g98,g94)
    c: Horizontal(g91,g95)
    c: Horizontal(g95,g99)
    c: Horizontal(g99,g103)
    c: DistanceX(g86,g90) = 11
    c: Horizontal(g90,g86)
    c: Horizontal(g91,g87)
    c: Tangent(g106,g109) = 1.5708
    c: Tangent(g106,g108) = -1.5708
    c: Tangent(g108,g107) = -1.5708
    c: Tangent(g109,g107) = 1.5708
    c: Vertical(g108)
    c: Equal(g106,g107)
    c: DistanceX(g102,g106) = 11
    c: Horizontal(g102,g106)
    c: Horizontal(g103,g107)
    c: Equal(g34,g106) = 3
    c: Horizontal(g110)
    c: Horizontal(g111)
    c: DistanceY(g110,g111) = 9
    c: Tangent(g112,g115) = 1.5708
    c: Tangent(g112,g114) = -1.5708
    c: Tangent(g114,g113) = -1.5708
    c: Tangent(g115,g113) = 1.5708
    c: Vertical(g114)
    c: Equal(g112,g113)
    c: Coincident(g112,g110)
    c: Equal(g2,g112) = 3
    c: PointOnObject(g113,g111)
    c: Tangent(g116,g119) = 1.5708
    c: Tangent(g116,g118) = -1.5708
    c: Tangent(g118,g117) = -1.5708
    c: Tangent(g119,g117) = 1.5708
    c: Vertical(g118)
    c: Equal(g116,g117)
    c: Equal(g112,g116) = 3
    c: DistanceX(g112,g116) = 11
    c: Horizontal(g116,g112)
    c: Tangent(g120,g123) = 1.5708
    c: Tangent(g120,g122) = -1.5708
    c: Tangent(g122,g121) = -1.5708
    c: Tangent(g123,g121) = 1.5708
    c: Vertical(g122)
    c: Equal(g120,g121)
    c: Equal(g112,g120) = 3
    c: Tangent(g124,g127) = 1.5708
    c: Tangent(g124,g126) = -1.5708
    c: Tangent(g126,g125) = -1.5708
    c: Tangent(g127,g125) = 1.5708
    c: Vertical(g126)
    c: Equal(g124,g125)
    c: Equal(g120,g124) = 3
    c: DistanceX(g120,g124) = 11
    c: Horizontal(g124,g120)
    c: DistanceX(g116,g120) = 11
    c: Horizontal(g120,g116)
    c: Horizontal(g113,g117)
    c: Horizontal(g117,g121)
    c: Horizontal(g121,g125)
    c: Tangent(g128,g131) = 1.5708
    c: Tangent(g128,g130) = -1.5708
    c: Tangent(g130,g129) = -1.5708
    c: Tangent(g131,g129) = 1.5708
    c: Vertical(g130)
    c: Equal(g128,g129)
    c: Equal(g112,g128) = 3
    c: Tangent(g132,g135) = 1.5708
    c: Tangent(g132,g134) = -1.5708
    c: Tangent(g134,g133) = -1.5708
    c: Tangent(g135,g133) = 1.5708
    c: Vertical(g134)
    c: Equal(g132,g133)
    c: Equal(g128,g132) = 3
    c: DistanceX(g128,g132) = 11
    c: Horizontal(g132,g128)
    c: Tangent(g136,g139) = 1.5708
    c: Tangent(g136,g138) = -1.5708
    c: Tangent(g138,g137) = -1.5708
    c: Tangent(g139,g137) = 1.5708
    c: Vertical(g138)
    c: Equal(g136,g137)
    c: Equal(g128,g136) = 3
    c: Tangent(g140,g143) = 1.5708
    c: Tangent(g140,g142) = -1.5708
    c: Tangent(g142,g141) = -1.5708
    c: Tangent(g143,g141) = 1.5708
    c: Vertical(g142)
    c: Equal(g140,g141)
    c: Equal(g136,g140) = 3
    c: DistanceX(g136,g140) = 11
    c: Horizontal(g140,g136)
    c: DistanceX(g132,g136) = 11
    c: Horizontal(g136,g132)
    c: Horizontal(g129,g133)
    c: Horizontal(g133,g137)
    c: Horizontal(g137,g141)
    c: DistanceX(g124,g128) = 11
    c: Horizontal(g128,g124)
    c: Horizontal(g129,g125)
    c: DistanceY(g110,g1) = 1.5
    c: DistanceX(g3,g112) = 5.5
    c: DistanceY(g72,g111) = 1.5
    c: Vertical(g3,g74)
    c: Horizontal(g144)
    c: Horizontal(g145)
    c: DistanceY(g144,g145) = 9
    c: Tangent(g146,g149) = 1.5708
    c: Tangent(g146,g148) = -1.5708
    c: Tangent(g148,g147) = -1.5708
    c: Tangent(g149,g147) = 1.5708
    c: Vertical(g148)
    c: Equal(g146,g147)
    c: Coincident(g146,g144)
    c: PointOnObject(g147,g145)
    c: Tangent(g150,g153) = 1.5708
    c: Tangent(g150,g152) = -1.5708
    c: Tangent(g152,g151) = -1.5708
    c: Tangent(g153,g151) = 1.5708
    c: Vertical(g152)
    c: Equal(g150,g151)
    c: Equal(g146,g150) = 3
    c: DistanceX(g146,g150) = 11
    c: Horizontal(g150,g146)
    c: Tangent(g154,g157) = 1.5708
    c: Tangent(g154,g156) = -1.5708
    c: Tangent(g156,g155) = -1.5708
    c: Tangent(g157,g155) = 1.5708
    c: Vertical(g156)
    c: Equal(g154,g155)
    c: Equal(g146,g154) = 3
    c: Tangent(g158,g161) = 1.5708
    c: Tangent(g158,g160) = -1.5708
    c: Tangent(g160,g159) = -1.5708
    c: Tangent(g161,g159) = 1.5708
    c: Vertical(g160)
    c: Equal(g158,g159)
    c: Equal(g154,g158) = 3
    c: DistanceX(g154,g158) = 11
    c: Horizontal(g158,g154)
    c: DistanceX(g150,g154) = 11
    c: Horizontal(g154,g150)
    c: Horizontal(g147,g151)
    c: Horizontal(g151,g155)
    c: Horizontal(g155,g159)
    c: Tangent(g162,g165) = 1.5708
    c: Tangent(g162,g164) = -1.5708
    c: Tangent(g164,g163) = -1.5708
    c: Tangent(g165,g163) = 1.5708
    c: Vertical(g164)
    c: Equal(g162,g163)
    c: Equal(g146,g162) = 3
    c: Tangent(g166,g169) = 1.5708
    c: Tangent(g166,g168) = -1.5708
    c: Tangent(g168,g167) = -1.5708
    c: Tangent(g169,g167) = 1.5708
    c: Vertical(g168)
    c: Equal(g166,g167)
    c: Equal(g162,g166) = 3
    c: DistanceX(g162,g166) = 11
    c: Horizontal(g166,g162)
    c: Tangent(g170,g173) = 1.5708
    c: Tangent(g170,g172) = -1.5708
    c: Tangent(g172,g171) = -1.5708
    c: Tangent(g173,g171) = 1.5708
    c: Vertical(g172)
    c: Equal(g170,g171)
    c: Equal(g162,g170) = 3
    c: Tangent(g174,g177) = 1.5708
    c: Tangent(g174,g176) = -1.5708
    c: Tangent(g176,g175) = -1.5708
    c: Tangent(g177,g175) = 1.5708
    c: Vertical(g176)
    c: Equal(g174,g175)
    c: Equal(g170,g174) = 3
    c: DistanceX(g170,g174) = 11
    c: Horizontal(g174,g170)
    c: DistanceX(g166,g170) = 11
    c: Horizontal(g170,g166)
    c: Horizontal(g163,g167)
    c: Horizontal(g167,g171)
    c: Horizontal(g171,g175)
    c: DistanceX(g158,g162) = 11
    c: Horizontal(g162,g158)
    c: Horizontal(g163,g159)
    c: DistanceX(g150,g150) = 3
    c: DistanceY(g144,g73) = 1.5
    c: Vertical(g113,g146)
    c: DistanceY(g38,g145) = 1.5
    c: DistanceY(g0,g-1) = 101
    c: DistanceX(g2,g-1) = 48
    c: Vertical(g79,g40)
FEATURE [Sketcher::SketchObject] Sketch005
  FullyConstrained = true
  MapMode = 5
  Placement = pos=(-1.0955e-12,2.25,0) rot=(0,0.707107,0.707107;3.14159rad)
  sketch-geometry (13):
    g0: LineSegment StartX=-51 StartY=93.5 StartZ=0 EndX=46 EndY=93.5 EndZ=0
    g1: LineSegment StartX=46 StartY=93.5 StartZ=0 EndX=46 EndY=-65.5 EndZ=0
    g2: LineSegment StartX=46 StartY=-65.5 StartZ=0 EndX=-51 EndY=-65.5 EndZ=0
    g3: LineSegment StartX=-51 StartY=-65.5 StartZ=0 EndX=-51 EndY=93.5 EndZ=0
    g4: GeomPoint X=-2.5 Y=14 Z=0
    g5: GeomPoint X=40.5 Y=89 Z=0
    g6: GeomPoint X=-44.5 Y=-63.5 Z=0
    g7: GeomPoint X=14 Y=36.5 Z=0
    g8: GeomPoint X=14 Y=-41.5 Z=0
    g9: Circle CenterX=-44.5 CenterY=-63.5 CenterZ=0 NormalX=0 NormalY=0 NormalZ=1 AngleXU=0 Radius=1.75
    g10: Circle CenterX=40.5 CenterY=89 CenterZ=0 NormalX=0 NormalY=0 NormalZ=1 AngleXU=0 Radius=1.75
    g11: Circle CenterX=14 CenterY=36.5 CenterZ=0 NormalX=0 NormalY=0 NormalZ=1 AngleXU=0 Radius=1.6
    g12: Circle CenterX=14 CenterY=-41.5 CenterZ=0 NormalX=0 NormalY=0 NormalZ=1 AngleXU=0 Radius=1.6
  constraints (29):
    c: Coincident(g0,g1)
    c: Coincident(g1,g2)
    c: Coincident(g2,g3)
    c: Coincident(g3,g0)
    c: Horizontal(g0)
    c: Horizontal(g2)
    c: Vertical(g1)
    c: Vertical(g3)
    c: DistanceY(g1,g1) = 159
    c: DistanceX(g0,g0) = 97
    c: Symmetric(g0,g1,g4)
    c: DistanceX(g6,g5) = 85
    c: DistanceY(g6,g5) = 152.5
    c: Vertical(g7,g8)
    c: DistanceY(g8,g7) = 78
    c: DistanceX(g7,g0) = 32
    c: DistanceY(g1,g8) = 24
    c: DistanceX(g2,g6) = 6.5
    c: DistanceY(g5,g0) = 4.5
    c: Coincident(g9,g6)
    c: Coincident(g10,g5)
    c: Equal(g10,g9)
    c: Coincident(g11,g7)
    c: Coincident(g12,g8)
    c: Equal(g12,g11)
    c: Diameter(g11) = 3.2
    c: Diameter(g9) = 3.5
    c: DistanceY(g-1,g4) = 14
    c: DistanceX(g4,g-1) = 2.5
FEATURE [Sketcher::SketchObject] Sketch007  label="Sketch007-rubber_feet"
  FullyConstrained = true
  MapMode = 5
  Placement = pos=(-1.0955e-12,2.25,0) rot=(0,0.707107,0.707107;3.14159rad)
  sketch-geometry (8):
    g0: LineSegment StartX=-60 StartY=92 StartZ=0 EndX=60 EndY=92 EndZ=0
    g1: LineSegment StartX=60 StartY=92 StartZ=0 EndX=60 EndY=-92 EndZ=0
    g2: LineSegment StartX=60 StartY=-92 StartZ=0 EndX=-60 EndY=-92 EndZ=0
    g3: LineSegment StartX=-60 StartY=-92 StartZ=0 EndX=-60 EndY=92 EndZ=0
    g4: Circle CenterX=-60 CenterY=92 CenterZ=0 NormalX=0 NormalY=0 NormalZ=1 AngleXU=0 Radius=3
    g5: Circle CenterX=60 CenterY=92 CenterZ=0 NormalX=0 NormalY=0 NormalZ=1 AngleXU=0 Radius=3
    g6: Circle CenterX=-60 CenterY=-92 CenterZ=0 NormalX=0 NormalY=0 NormalZ=1 AngleXU=0 Radius=3
    g7: Circle CenterX=60 CenterY=-92 CenterZ=0 NormalX=0 NormalY=0 NormalZ=1 AngleXU=0 Radius=3
  constraints (19):
    c: Coincident(g0,g1)
    c: Coincident(g1,g2)
    c: Coincident(g2,g3)
    c: Coincident(g3,g0)
    c: Horizontal(g0)
    c: Horizontal(g2)
    c: Vertical(g1)
    c: Vertical(g3)
    c: Symmetric(g0,g1,g-1)
    c: DistanceX(g2,g2) = 120
    c: DistanceY(g1,g1) = 184
    c: Equal(g4,g5)
    c: Equal(g5,g7)
    c: Equal(g7,g6)
    c: Coincident(g4,g0)
    c: Coincident(g5,g0)
    c: Coincident(g7,g1)
    c: Coincident(g6,g2)
    c: Diameter(g4) = 6
FEATURE [Part::Feature] Pocket006001  label="Bottom_Cap_w_back_vent_slots001"
  shape: bbox 152.4 x 4.293 x 220 mm, 458 faces (baked)
FEATURE [Part::Feature] Part__Feature074  label="POF-50185_push-on_feet-FL"
  Placement = pos=(-60,11,92) rot=(0,0,1;0rad)
  shape: bbox 13.72 x 15.56 x 13.72 mm, 13 faces (baked)
FEATURE [Part::Feature] Part__Feature075  label="POF-50185_push-on_feet-FR"
  Placement = pos=(60,11,92) rot=(0,0,1;0rad)
  shape: bbox 13.72 x 15.56 x 13.72 mm, 13 faces (baked)
FEATURE [Part::Feature] Part__Feature076  label="POF-50185_push-on_feet-RL"
  Placement = pos=(-60,11,-92) rot=(0,0,1;0rad)
  shape: bbox 13.72 x 15.56 x 13.72 mm, 13 faces (baked)
FEATURE [Part::Feature] Part__Feature077  label="POF-50185_push-on_feet-RR"
  Placement = pos=(60,11,-92) rot=(0,0,1;0rad)
  shape: bbox 13.72 x 15.56 x 13.72 mm, 13 faces (baked)
FEATURE [App::DocumentObjectGroup] Group  label="BottomPlate_w_feet_PSU_holes_vents"
  Group = -> [Sketch008,Sketch009,Sketch010,Sketch005,Sketch007,Pocket006001,Part__Feature074,Part__Feature075,Part__Feature077,Part__Feature076]
